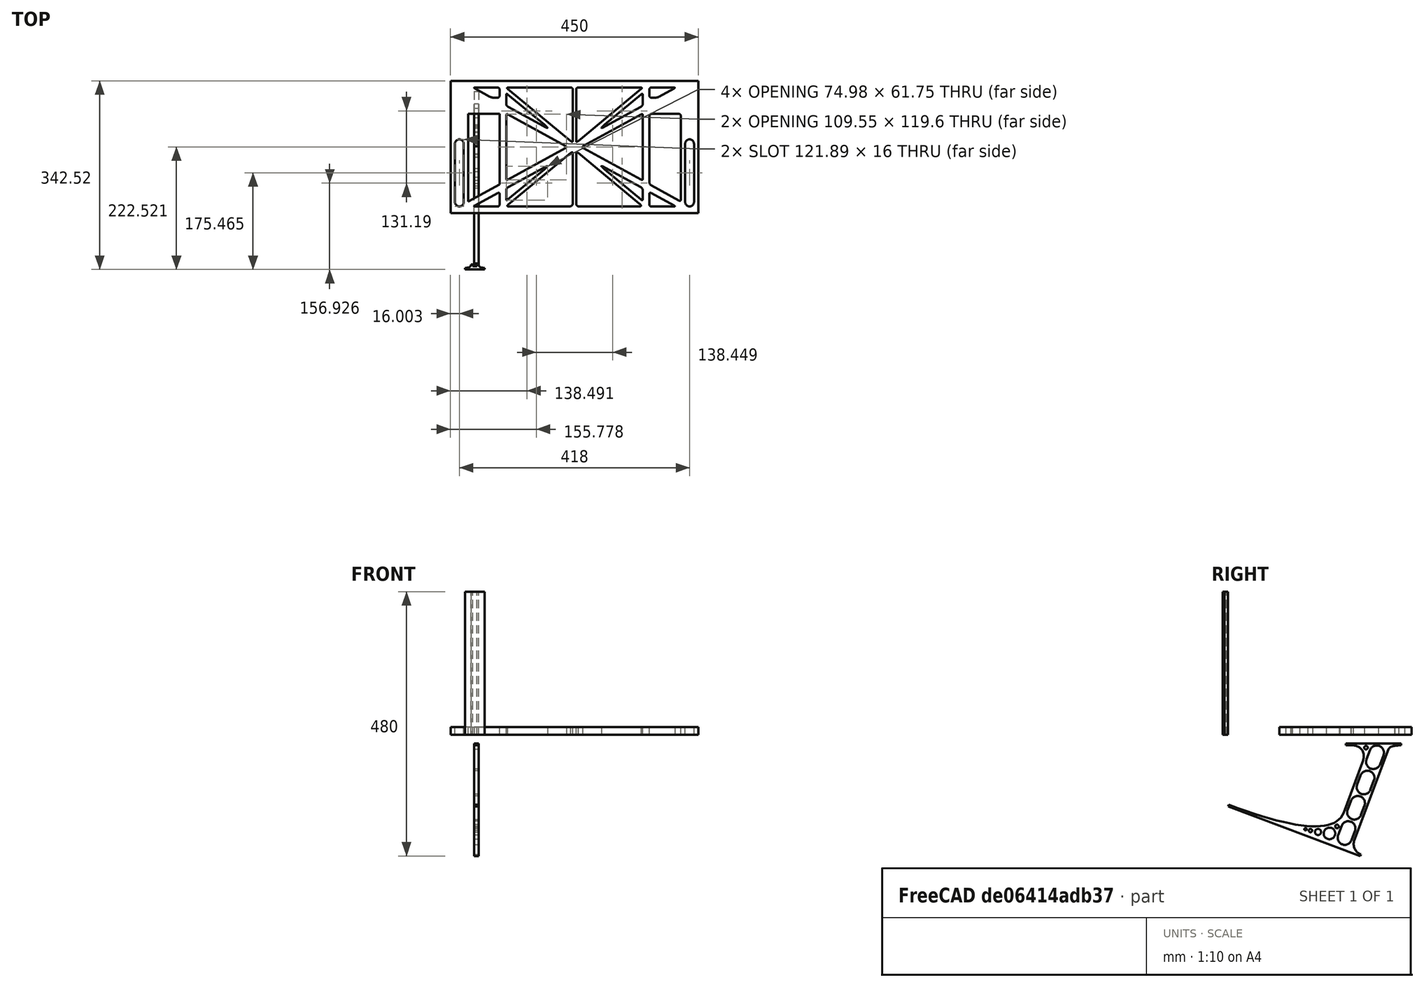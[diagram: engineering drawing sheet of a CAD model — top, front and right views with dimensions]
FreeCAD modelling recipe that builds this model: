
FCSTD DOCUMENT  (FreeCAD 0.19R0.19.2)
Label: laptopStand140FCStd
License: All rights reserved
LicenseURL: http://en.wikipedia.org/wiki/All_rights_reserved
objects: Sketcher::SketchObject×4, Part::Extrusion×3
note: 7 computed .brp shape members not serialized (recipe doc carries the construction recipe); baked Part::Feature solids carry a one-line shape summary decoded from their .brp

FEATURE [Sketcher::SketchObject] Sketch
  FullyConstrained = false
  sketch-geometry (349):
    g0: LineSegment StartX=-10.9272 StartY=-82.7794 StartZ=0 EndX=46.0728 EndY=-51.4823 EndZ=0
    g1: LineSegment StartX=-10.9272 StartY=76.4095 StartZ=0 EndX=-10.9272 EndY=-82.7794 EndZ=0
    g2: LineSegment StartX=46.0728 StartY=76.4095 StartZ=0 EndX=46.0728 EndY=-51.4823 EndZ=0
    g3: LineSegment StartX=-42.9272 StartY=136.221 StartZ=0 EndX=-42.9272 EndY=-103.779 EndZ=0
    g4: LineSegment StartX=407.073 StartY=136.221 StartZ=0 EndX=407.073 EndY=-103.779 EndZ=0
    g5: ArcOfCircle CenterX=-26.9272 CenterY=-83.7794 CenterZ=0 NormalX=0 NormalY=0 NormalZ=1 AngleXU=0 Radius=8 StartAngle=3.14159 EndAngle=6.28319
    g6: ArcOfCircle CenterX=391.073 CenterY=22.1087 CenterZ=0 NormalX=0 NormalY=0 NormalZ=1 AngleXU=0 Radius=8 StartAngle=-4.4e-15 EndAngle=3.14159
    g7: LineSegment StartX=399.073 StartY=22.1087 StartZ=0 EndX=399.073 EndY=-83.7794 EndZ=0
    g8: LineSegment StartX=383.073 StartY=22.1087 StartZ=0 EndX=383.073 EndY=-83.7794 EndZ=0
    g9: ArcOfCircle CenterX=391.073 CenterY=-83.7794 CenterZ=0 NormalX=0 NormalY=0 NormalZ=1 AngleXU=0 Radius=8 StartAngle=3.14159 EndAngle=6.28319
    g10: Circle CenterX=175.022 CenterY=27.0628 CenterZ=0 NormalX=0 NormalY=0 NormalZ=1 AngleXU=0 Radius=1
    g11: Circle CenterX=179.022 CenterY=24.8665 CenterZ=0 NormalX=0 NormalY=0 NormalZ=1 AngleXU=0 Radius=1
    g12: Circle CenterX=179.022 CenterY=27.0628 CenterZ=0 NormalX=0 NormalY=0 NormalZ=1 AngleXU=0 Radius=1
    g13: BSplineCurve PolesCount=3 KnotsCount=2 Degree=2 IsPeriodic=0
    g14: GeomPoint X=175.022 Y=27.0628 Z=0
    g15: GeomPoint X=179.022 Y=27.0628 Z=0
    g16: Circle CenterX=189.124 CenterY=27.0628 CenterZ=0 NormalX=0 NormalY=0 NormalZ=1 AngleXU=0 Radius=1
    g17: Circle CenterX=185.124 CenterY=24.8665 CenterZ=0 NormalX=0 NormalY=0 NormalZ=1 AngleXU=0 Radius=1
    g18: Circle CenterX=185.124 CenterY=27.0628 CenterZ=0 NormalX=0 NormalY=0 NormalZ=1 AngleXU=0 Radius=1
    g19: BSplineCurve PolesCount=3 KnotsCount=2 Degree=2 IsPeriodic=0
    g20: GeomPoint X=189.124 Y=27.0628 Z=0
    g21: GeomPoint X=185.124 Y=27.0628 Z=0
    g22: Circle CenterX=175.022 CenterY=5.37834 CenterZ=0 NormalX=0 NormalY=0 NormalZ=1 AngleXU=0 Radius=1
    g23: Circle CenterX=179.022 CenterY=7.57463 CenterZ=0 NormalX=0 NormalY=0 NormalZ=1 AngleXU=0 Radius=1
    g24: Circle CenterX=179.022 CenterY=5.34704 CenterZ=0 NormalX=0 NormalY=0 NormalZ=1 AngleXU=0 Radius=1
    g25: BSplineCurve PolesCount=3 KnotsCount=2 Degree=2 IsPeriodic=0
    g26: GeomPoint X=175.022 Y=5.37834 Z=0
    g27: GeomPoint X=179.022 Y=5.34704 Z=0
    g28: Circle CenterX=189.124 CenterY=5.37834 CenterZ=0 NormalX=0 NormalY=0 NormalZ=1 AngleXU=0 Radius=1
    g29: Circle CenterX=185.124 CenterY=7.57463 CenterZ=0 NormalX=0 NormalY=0 NormalZ=1 AngleXU=0 Radius=1
    g30: Circle CenterX=185.124 CenterY=5.34704 CenterZ=0 NormalX=0 NormalY=0 NormalZ=1 AngleXU=0 Radius=1
    g31: BSplineCurve PolesCount=3 KnotsCount=2 Degree=2 IsPeriodic=0
    g32: GeomPoint X=189.124 Y=5.37834 Z=0
    g33: GeomPoint X=185.124 Y=5.34704 Z=0
    g34: Circle CenterX=165.871 CenterY=18.1458 CenterZ=0 NormalX=0 NormalY=0 NormalZ=1 AngleXU=0 Radius=1
    g35: Circle CenterX=169.377 CenterY=16.2206 CenterZ=0 NormalX=0 NormalY=0 NormalZ=1 AngleXU=0 Radius=1
    g36: Circle CenterX=165.871 CenterY=14.2954 CenterZ=0 NormalX=0 NormalY=0 NormalZ=1 AngleXU=0 Radius=1
    g37: BSplineCurve PolesCount=3 KnotsCount=2 Degree=2 IsPeriodic=0
    g38: GeomPoint X=165.871 Y=18.1458 Z=0
    g39: GeomPoint X=165.871 Y=14.2954 Z=0
    g40: Circle CenterX=198.275 CenterY=18.1458 CenterZ=0 NormalX=0 NormalY=0 NormalZ=1 AngleXU=0 Radius=1
    g41: Circle CenterX=194.768 CenterY=16.2206 CenterZ=0 NormalX=0 NormalY=0 NormalZ=1 AngleXU=0 Radius=1
    g42: Circle CenterX=198.275 CenterY=14.2954 CenterZ=0 NormalX=0 NormalY=0 NormalZ=1 AngleXU=0 Radius=1
    g43: BSplineCurve PolesCount=3 KnotsCount=2 Degree=2 IsPeriodic=0
    g44: GeomPoint X=198.275 Y=18.1458 Z=0
    g45: GeomPoint X=198.275 Y=14.2954 Z=0
    g46: LineSegment StartX=407.073 StartY=-103.779 StartZ=0 EndX=-42.9272 EndY=-103.779 EndZ=0
    g47: LineSegment StartX=407.073 StartY=136.221 StartZ=0 EndX=-42.9272 EndY=136.221 EndZ=0
    g48: LineSegment StartX=46.0728 StartY=76.4095 StartZ=0 EndX=-10.9272 EndY=76.4095 EndZ=0
    g49: Circle CenterX=125.607 CenterY=54.1951 CenterZ=0 NormalX=0 NormalY=0 NormalZ=1 AngleXU=0 Radius=1
    g50: Circle CenterX=139.632 CenterY=46.4944 CenterZ=0 NormalX=0 NormalY=0 NormalZ=1 AngleXU=0 Radius=1
    g51: Circle CenterX=127.326 CenterY=56.7187 CenterZ=0 NormalX=0 NormalY=0 NormalZ=1 AngleXU=0 Radius=1
    g52: BSplineCurve PolesCount=3 KnotsCount=2 Degree=2 IsPeriodic=0
    g53: GeomPoint X=125.607 Y=54.1951 Z=0
    g54: GeomPoint X=127.326 Y=56.7187 Z=0
    g55: Circle CenterX=236.821 CenterY=56.7187 CenterZ=0 NormalX=0 NormalY=0 NormalZ=1 AngleXU=0 Radius=1
    g56: Circle CenterX=224.513 CenterY=46.4944 CenterZ=0 NormalX=0 NormalY=0 NormalZ=1 AngleXU=0 Radius=1
    g57: Circle CenterX=238.538 CenterY=54.1951 CenterZ=0 NormalX=0 NormalY=0 NormalZ=1 AngleXU=0 Radius=1
    g58: BSplineCurve PolesCount=3 KnotsCount=2 Degree=2 IsPeriodic=0
    g59: GeomPoint X=236.821 Y=56.7187 Z=0
    g60: GeomPoint X=238.538 Y=54.1951 Z=0
    g61: Circle CenterX=238.538 CenterY=-21.7539 CenterZ=0 NormalX=0 NormalY=0 NormalZ=1 AngleXU=0 Radius=1
    g62: Circle CenterX=224.513 CenterY=-14.0532 CenterZ=0 NormalX=0 NormalY=0 NormalZ=1 AngleXU=0 Radius=1
    g63: Circle CenterX=236.821 CenterY=-24.2775 CenterZ=0 NormalX=0 NormalY=0 NormalZ=1 AngleXU=0 Radius=1
    g64: BSplineCurve PolesCount=3 KnotsCount=2 Degree=2 IsPeriodic=0
    g65: GeomPoint X=238.538 Y=-21.7539 Z=0
    g66: GeomPoint X=236.821 Y=-24.2775 Z=0
    g67: Circle CenterX=125.607 CenterY=-21.7539 CenterZ=0 NormalX=0 NormalY=0 NormalZ=1 AngleXU=0 Radius=1
    g68: Circle CenterX=139.632 CenterY=-14.0532 CenterZ=0 NormalX=0 NormalY=0 NormalZ=1 AngleXU=0 Radius=1
    g69: Circle CenterX=127.325 CenterY=-24.2775 CenterZ=0 NormalX=0 NormalY=0 NormalZ=1 AngleXU=0 Radius=1
    g70: BSplineCurve PolesCount=3 KnotsCount=2 Degree=2 IsPeriodic=0
    g71: GeomPoint X=125.607 Y=-21.7539 Z=0
    g72: GeomPoint X=127.325 Y=-24.2775 Z=0
    g73: Circle CenterX=302.996 CenterY=111.695 CenterZ=0 NormalX=0 NormalY=0 NormalZ=1 AngleXU=0 Radius=1
    g74: Circle CenterX=306.073 CenterY=114.251 CenterZ=0 NormalX=0 NormalY=0 NormalZ=1 AngleXU=0 Radius=1
    g75: Circle CenterX=306.073 CenterY=110.251 CenterZ=0 NormalX=0 NormalY=0 NormalZ=1 AngleXU=0 Radius=1
    g76: BSplineCurve PolesCount=3 KnotsCount=2 Degree=2 IsPeriodic=0
    g77: GeomPoint X=302.996 Y=111.695 Z=0
    g78: GeomPoint X=306.073 Y=110.251 Z=0
    g79: Circle CenterX=306.073 CenterY=95.2763 CenterZ=0 NormalX=0 NormalY=0 NormalZ=1 AngleXU=0 Radius=1
    g80: Circle CenterX=306.073 CenterY=91.2763 CenterZ=0 NormalX=0 NormalY=0 NormalZ=1 AngleXU=0 Radius=1
    g81: Circle CenterX=302.567 CenterY=89.3511 CenterZ=0 NormalX=0 NormalY=0 NormalZ=1 AngleXU=0 Radius=1
    g82: BSplineCurve PolesCount=3 KnotsCount=2 Degree=2 IsPeriodic=0
    g83: GeomPoint X=306.073 Y=95.2763 Z=0
    g84: GeomPoint X=302.567 Y=89.3511 Z=0
    g85: LineSegment StartX=306.073 StartY=110.251 StartZ=0 EndX=306.073 EndY=95.2763 EndZ=0
    g86: LineSegment StartX=302.996 StartY=111.695 StartZ=0 EndX=236.821 EndY=56.7187 EndZ=0
    g87: LineSegment StartX=238.538 StartY=54.1951 StartZ=0 EndX=302.567 EndY=89.3511 EndZ=0
    g88: Circle CenterX=61.1496 CenterY=111.695 CenterZ=0 NormalX=0 NormalY=0 NormalZ=1 AngleXU=0 Radius=1
    g89: Circle CenterX=58.0728 CenterY=114.251 CenterZ=0 NormalX=0 NormalY=0 NormalZ=1 AngleXU=0 Radius=1
    g90: Circle CenterX=58.0728 CenterY=110.251 CenterZ=0 NormalX=0 NormalY=0 NormalZ=1 AngleXU=0 Radius=1
    g91: BSplineCurve PolesCount=3 KnotsCount=2 Degree=2 IsPeriodic=0
    g92: GeomPoint X=61.1496 Y=111.695 Z=0
    g93: GeomPoint X=58.0728 Y=110.251 Z=0
    g94: Circle CenterX=61.5791 CenterY=89.3511 CenterZ=0 NormalX=0 NormalY=0 NormalZ=1 AngleXU=0 Radius=1
    g95: Circle CenterX=58.0728 CenterY=91.2763 CenterZ=0 NormalX=0 NormalY=0 NormalZ=1 AngleXU=0 Radius=1
    g96: Circle CenterX=58.0728 CenterY=95.2763 CenterZ=0 NormalX=0 NormalY=0 NormalZ=1 AngleXU=0 Radius=1
    g97: BSplineCurve PolesCount=3 KnotsCount=2 Degree=2 IsPeriodic=0
    g98: GeomPoint X=61.5791 Y=89.3511 Z=0
    g99: GeomPoint X=58.0728 Y=95.2763 Z=0
    g100: LineSegment StartX=58.0728 StartY=110.251 StartZ=0 EndX=58.0728 EndY=95.2763 EndZ=0
    g101: LineSegment StartX=61.1496 StartY=111.695 StartZ=0 EndX=127.326 EndY=56.7187 EndZ=0
    g102: LineSegment StartX=125.607 StartY=54.1951 StartZ=0 EndX=61.5791 EndY=89.3511 EndZ=0
    g103: Circle CenterX=61.5791 CenterY=-56.9099 CenterZ=0 NormalX=0 NormalY=0 NormalZ=1 AngleXU=0 Radius=1
    g104: Circle CenterX=58.0728 CenterY=-58.8351 CenterZ=0 NormalX=0 NormalY=0 NormalZ=1 AngleXU=0 Radius=1
    g105: Circle CenterX=58.0728 CenterY=-62.8351 CenterZ=0 NormalX=0 NormalY=0 NormalZ=1 AngleXU=0 Radius=1
    g106: BSplineCurve PolesCount=3 KnotsCount=2 Degree=2 IsPeriodic=0
    g107: GeomPoint X=61.5791 Y=-56.9099 Z=0
    g108: GeomPoint X=58.0728 Y=-62.8351 Z=0
    g109: Circle CenterX=58.0728 CenterY=-77.8102 CenterZ=0 NormalX=0 NormalY=0 NormalZ=1 AngleXU=0 Radius=1
    g110: Circle CenterX=58.0728 CenterY=-81.8102 CenterZ=0 NormalX=0 NormalY=0 NormalZ=1 AngleXU=0 Radius=1
    g111: Circle CenterX=61.1496 CenterY=-79.2541 CenterZ=0 NormalX=0 NormalY=0 NormalZ=1 AngleXU=0 Radius=1
    g112: BSplineCurve PolesCount=3 KnotsCount=2 Degree=2 IsPeriodic=0
    g113: GeomPoint X=58.0728 Y=-77.8102 Z=0
    g114: GeomPoint X=61.1496 Y=-79.2541 Z=0
    g115: LineSegment StartX=58.0728 StartY=-62.8351 StartZ=0 EndX=58.0728 EndY=-77.8102 EndZ=0
    g116: LineSegment StartX=61.1496 StartY=-79.2541 StartZ=0 EndX=127.325 EndY=-24.2775 EndZ=0
    g117: LineSegment StartX=125.607 StartY=-21.7539 StartZ=0 EndX=61.5791 EndY=-56.9099 EndZ=0
    g118: Circle CenterX=302.567 CenterY=-56.9099 CenterZ=0 NormalX=0 NormalY=0 NormalZ=1 AngleXU=0 Radius=1
    g119: Circle CenterX=306.073 CenterY=-58.8351 CenterZ=0 NormalX=0 NormalY=0 NormalZ=1 AngleXU=0 Radius=1
    g120: Circle CenterX=306.073 CenterY=-62.8351 CenterZ=0 NormalX=0 NormalY=0 NormalZ=1 AngleXU=0 Radius=1
    g121: BSplineCurve PolesCount=3 KnotsCount=2 Degree=2 IsPeriodic=0
    g122: GeomPoint X=302.567 Y=-56.9099 Z=0
    g123: GeomPoint X=306.073 Y=-62.8351 Z=0
    g124: Circle CenterX=302.996 CenterY=-79.2541 CenterZ=0 NormalX=0 NormalY=0 NormalZ=1 AngleXU=0 Radius=1
    g125: Circle CenterX=306.073 CenterY=-81.8102 CenterZ=0 NormalX=0 NormalY=0 NormalZ=1 AngleXU=0 Radius=1
    g126: Circle CenterX=306.073 CenterY=-77.8102 CenterZ=0 NormalX=0 NormalY=0 NormalZ=1 AngleXU=0 Radius=1
    g127: BSplineCurve PolesCount=3 KnotsCount=2 Degree=2 IsPeriodic=0
    g128: GeomPoint X=302.996 Y=-79.2541 Z=0
    g129: GeomPoint X=306.073 Y=-77.8102 Z=0
    g130: LineSegment StartX=306.073 StartY=-62.8351 StartZ=0 EndX=306.073 EndY=-77.8102 EndZ=0
    g131: LineSegment StartX=302.996 StartY=-79.2541 StartZ=0 EndX=236.821 EndY=-24.2775 EndZ=0
    g132: LineSegment StartX=238.538 StartY=-21.7539 StartZ=0 EndX=302.567 EndY=-56.9099 EndZ=0
    g133: Circle CenterX=61.6457 CenterY=-88.8112 CenterZ=0 NormalX=0 NormalY=0 NormalZ=1 AngleXU=0 Radius=1
    g134: Circle CenterX=58.0728 CenterY=-91.7794 CenterZ=0 NormalX=0 NormalY=0 NormalZ=1 AngleXU=0 Radius=1
    g135: Circle CenterX=63.9135 CenterY=-91.7794 CenterZ=0 NormalX=0 NormalY=0 NormalZ=1 AngleXU=0 Radius=1
    g136: BSplineCurve PolesCount=3 KnotsCount=2 Degree=2 IsPeriodic=0
    g137: GeomPoint X=61.6457 Y=-88.8112 Z=0
    g138: GeomPoint X=63.9135 Y=-91.7794 Z=0
    g139: Circle CenterX=179.022 CenterY=-85.8163 CenterZ=0 NormalX=0 NormalY=0 NormalZ=1 AngleXU=0 Radius=1
    g140: Circle CenterX=179.022 CenterY=-91.7794 CenterZ=0 NormalX=0 NormalY=0 NormalZ=1 AngleXU=0 Radius=1
    g141: Circle CenterX=171.895 CenterY=-91.7794 CenterZ=0 NormalX=0 NormalY=0 NormalZ=1 AngleXU=0 Radius=1
    g142: BSplineCurve PolesCount=3 KnotsCount=2 Degree=2 IsPeriodic=0
    g143: GeomPoint X=179.022 Y=-85.8163 Z=0
    g144: GeomPoint X=171.895 Y=-91.7794 Z=0
    g145: Circle CenterX=185.124 CenterY=-86.2028 CenterZ=0 NormalX=0 NormalY=0 NormalZ=1 AngleXU=0 Radius=1
    g146: Circle CenterX=185.124 CenterY=-91.7794 CenterZ=0 NormalX=0 NormalY=0 NormalZ=1 AngleXU=0 Radius=1
    g147: Circle CenterX=191.747 CenterY=-91.7794 CenterZ=0 NormalX=0 NormalY=0 NormalZ=1 AngleXU=0 Radius=1
    g148: BSplineCurve PolesCount=3 KnotsCount=2 Degree=2 IsPeriodic=0
    g149: GeomPoint X=185.124 Y=-86.2028 Z=0
    g150: GeomPoint X=191.747 Y=-91.7794 Z=0
    g151: Circle CenterX=299.888 CenterY=-86.6413 CenterZ=0 NormalX=0 NormalY=0 NormalZ=1 AngleXU=0 Radius=1
    g152: Circle CenterX=306.073 CenterY=-91.7794 CenterZ=0 NormalX=0 NormalY=0 NormalZ=1 AngleXU=0 Radius=1
    g153: Circle CenterX=298.776 CenterY=-91.7794 CenterZ=0 NormalX=0 NormalY=0 NormalZ=1 AngleXU=0 Radius=1
    g154: BSplineCurve PolesCount=3 KnotsCount=2 Degree=2 IsPeriodic=0
    g155: GeomPoint X=299.888 Y=-86.6413 Z=0
    g156: GeomPoint X=298.776 Y=-91.7794 Z=0
    g157: LineSegment StartX=189.124 StartY=5.37834 StartZ=0 EndX=299.888 EndY=-86.6413 EndZ=0
    g158: LineSegment StartX=298.776 StartY=-91.7794 StartZ=0 EndX=191.747 EndY=-91.7794 EndZ=0
    g159: LineSegment StartX=185.124 StartY=-86.2028 StartZ=0 EndX=185.124 EndY=5.34704 EndZ=0
    g160: LineSegment StartX=179.022 StartY=5.34704 StartZ=0 EndX=179.022 EndY=-85.8163 EndZ=0
    g161: LineSegment StartX=171.895 StartY=-91.7794 StartZ=0 EndX=63.9135 EndY=-91.7794 EndZ=0
    g162: LineSegment StartX=61.6457 StartY=-88.8112 StartZ=0 EndX=175.022 EndY=5.37834 EndZ=0
    g163: Circle CenterX=302.073 CenterY=124.221 CenterZ=0 NormalX=0 NormalY=0 NormalZ=1 AngleXU=0 Radius=1
    g164: Circle CenterX=306.073 CenterY=124.221 CenterZ=0 NormalX=0 NormalY=0 NormalZ=1 AngleXU=0 Radius=1
    g165: Circle CenterX=302.996 CenterY=121.665 CenterZ=0 NormalX=0 NormalY=0 NormalZ=1 AngleXU=0 Radius=1
    g166: BSplineCurve PolesCount=3 KnotsCount=2 Degree=2 IsPeriodic=0
    g167: GeomPoint X=302.073 Y=124.221 Z=0
    g168: GeomPoint X=302.996 Y=121.665 Z=0
    g169: Circle CenterX=189.124 CenterY=124.221 CenterZ=0 NormalX=0 NormalY=0 NormalZ=1 AngleXU=0 Radius=1
    g170: Circle CenterX=185.124 CenterY=124.221 CenterZ=0 NormalX=0 NormalY=0 NormalZ=1 AngleXU=0 Radius=1
    g171: Circle CenterX=185.124 CenterY=120.221 CenterZ=0 NormalX=0 NormalY=0 NormalZ=1 AngleXU=0 Radius=1
    g172: BSplineCurve PolesCount=3 KnotsCount=2 Degree=2 IsPeriodic=0
    g173: GeomPoint X=189.124 Y=124.221 Z=0
    g174: GeomPoint X=185.124 Y=120.221 Z=0
    g175: Circle CenterX=175.022 CenterY=124.221 CenterZ=0 NormalX=0 NormalY=0 NormalZ=1 AngleXU=0 Radius=1
    g176: Circle CenterX=179.022 CenterY=124.221 CenterZ=0 NormalX=0 NormalY=0 NormalZ=1 AngleXU=0 Radius=1
    g177: Circle CenterX=179.022 CenterY=120.221 CenterZ=0 NormalX=0 NormalY=0 NormalZ=1 AngleXU=0 Radius=1
    g178: BSplineCurve PolesCount=3 KnotsCount=2 Degree=2 IsPeriodic=0
    g179: GeomPoint X=175.022 Y=124.221 Z=0
    g180: GeomPoint X=179.022 Y=120.221 Z=0
    g181: Circle CenterX=62.0728 CenterY=124.221 CenterZ=0 NormalX=0 NormalY=0 NormalZ=1 AngleXU=0 Radius=1
    g182: Circle CenterX=58.0728 CenterY=124.221 CenterZ=0 NormalX=0 NormalY=0 NormalZ=1 AngleXU=0 Radius=1
    g183: Circle CenterX=61.1496 CenterY=121.665 CenterZ=0 NormalX=0 NormalY=0 NormalZ=1 AngleXU=0 Radius=1
    g184: BSplineCurve PolesCount=3 KnotsCount=2 Degree=2 IsPeriodic=0
    g185: GeomPoint X=62.0728 Y=124.221 Z=0
    g186: GeomPoint X=61.1496 Y=121.665 Z=0
    g187: LineSegment StartX=62.0728 StartY=124.221 StartZ=0 EndX=175.022 EndY=124.221 EndZ=0
    g188: LineSegment StartX=179.022 StartY=120.221 StartZ=0 EndX=179.022 EndY=27.0628 EndZ=0
    g189: LineSegment StartX=185.124 StartY=27.0628 StartZ=0 EndX=185.124 EndY=120.221 EndZ=0
    g190: LineSegment StartX=189.124 StartY=124.221 StartZ=0 EndX=302.073 EndY=124.221 EndZ=0
    g191: LineSegment StartX=302.996 StartY=121.665 StartZ=0 EndX=189.124 EndY=27.0628 EndZ=0
    g192: LineSegment StartX=175.022 StartY=27.0628 StartZ=0 EndX=61.1496 EndY=121.665 EndZ=0
    g193: Circle CenterX=61.5791 CenterY=75.4095 CenterZ=0 NormalX=0 NormalY=0 NormalZ=1 AngleXU=0 Radius=1
    g194: Circle CenterX=58.0728 CenterY=77.3346 CenterZ=0 NormalX=0 NormalY=0 NormalZ=1 AngleXU=0 Radius=1
    g195: Circle CenterX=58.0728 CenterY=73.3346 CenterZ=0 NormalX=0 NormalY=0 NormalZ=1 AngleXU=0 Radius=1
    g196: BSplineCurve PolesCount=3 KnotsCount=2 Degree=2 IsPeriodic=0
    g197: GeomPoint X=61.5791 Y=75.4095 Z=0
    g198: GeomPoint X=58.0728 Y=73.3346 Z=0
    g199: Circle CenterX=58.0728 CenterY=-40.8935 CenterZ=0 NormalX=0 NormalY=0 NormalZ=1 AngleXU=0 Radius=1
    g200: Circle CenterX=58.0728 CenterY=-44.8935 CenterZ=0 NormalX=0 NormalY=0 NormalZ=1 AngleXU=0 Radius=1
    g201: Circle CenterX=61.5791 CenterY=-42.9683 CenterZ=0 NormalX=0 NormalY=0 NormalZ=1 AngleXU=0 Radius=1
    g202: BSplineCurve PolesCount=3 KnotsCount=2 Degree=2 IsPeriodic=0
    g203: GeomPoint X=58.0728 Y=-40.8935 Z=0
    g204: GeomPoint X=61.5791 Y=-42.9683 Z=0
    g205: LineSegment StartX=61.5791 StartY=-42.9683 StartZ=0 EndX=165.871 EndY=14.2954 EndZ=0
    g206: LineSegment StartX=165.871 StartY=18.1458 StartZ=0 EndX=61.5791 EndY=75.4095 EndZ=0
    g207: LineSegment StartX=58.0728 StartY=73.3346 StartZ=0 EndX=58.0728 EndY=-40.8935 EndZ=0
    g208: Circle CenterX=302.567 CenterY=-42.9683 CenterZ=0 NormalX=0 NormalY=0 NormalZ=1 AngleXU=0 Radius=1
    g209: Circle CenterX=306.073 CenterY=-44.8935 CenterZ=0 NormalX=0 NormalY=0 NormalZ=1 AngleXU=0 Radius=1
    g210: Circle CenterX=306.073 CenterY=-40.8935 CenterZ=0 NormalX=0 NormalY=0 NormalZ=1 AngleXU=0 Radius=1
    g211: BSplineCurve PolesCount=3 KnotsCount=2 Degree=2 IsPeriodic=0
    g212: GeomPoint X=302.567 Y=-42.9683 Z=0
    g213: GeomPoint X=306.073 Y=-40.8935 Z=0
    g214: Circle CenterX=306.073 CenterY=73.3346 CenterZ=0 NormalX=0 NormalY=0 NormalZ=1 AngleXU=0 Radius=1
    g215: Circle CenterX=306.073 CenterY=77.3346 CenterZ=0 NormalX=0 NormalY=0 NormalZ=1 AngleXU=0 Radius=1
    g216: Circle CenterX=302.567 CenterY=75.4095 CenterZ=0 NormalX=0 NormalY=0 NormalZ=1 AngleXU=0 Radius=1
    g217: BSplineCurve PolesCount=3 KnotsCount=2 Degree=2 IsPeriodic=0
    g218: GeomPoint X=306.073 Y=73.3346 Z=0
    g219: GeomPoint X=302.567 Y=75.4095 Z=0
    g220: LineSegment StartX=302.567 StartY=-42.9683 StartZ=0 EndX=198.275 EndY=14.2954 EndZ=0
    g221: LineSegment StartX=198.275 StartY=18.1458 StartZ=0 EndX=302.567 EndY=75.4095 EndZ=0
    g222: LineSegment StartX=306.073 StartY=73.3346 StartZ=0 EndX=306.073 EndY=-40.8935 EndZ=0
    g223: LineSegment StartX=322.073 StartY=105.865 StartZ=0 EndX=328.643 EndY=105.865 EndZ=0
    g224: LineSegment StartX=318.073 StartY=120.221 StartZ=0 EndX=318.073 EndY=109.865 EndZ=0
    g225: LineSegment StartX=336.157 StartY=107.779 StartZ=0 EndX=362.567 EndY=122.294 EndZ=0
    g226: Circle CenterX=362.073 CenterY=124.221 CenterZ=0 NormalX=0 NormalY=0 NormalZ=1 AngleXU=0 Radius=1
    g227: Circle CenterX=366.073 CenterY=124.221 CenterZ=0 NormalX=0 NormalY=0 NormalZ=1 AngleXU=0 Radius=1
    g228: Circle CenterX=362.567 CenterY=122.294 CenterZ=0 NormalX=0 NormalY=0 NormalZ=1 AngleXU=0 Radius=1
    g229: BSplineCurve PolesCount=3 KnotsCount=2 Degree=2 IsPeriodic=0
    g230: GeomPoint X=362.073 Y=124.221 Z=0
    g231: GeomPoint X=362.567 Y=122.294 Z=0
    g232: Circle CenterX=322.073 CenterY=124.221 CenterZ=0 NormalX=0 NormalY=0 NormalZ=1 AngleXU=0 Radius=1
    g233: Circle CenterX=318.073 CenterY=124.221 CenterZ=0 NormalX=0 NormalY=0 NormalZ=1 AngleXU=0 Radius=1
    g234: Circle CenterX=318.073 CenterY=120.221 CenterZ=0 NormalX=0 NormalY=0 NormalZ=1 AngleXU=0 Radius=1
    g235: BSplineCurve PolesCount=3 KnotsCount=2 Degree=2 IsPeriodic=0
    g236: GeomPoint X=322.073 Y=124.221 Z=0
    g237: GeomPoint X=318.073 Y=120.221 Z=0
    g238: Circle CenterX=322.073 CenterY=105.865 CenterZ=0 NormalX=0 NormalY=0 NormalZ=1 AngleXU=0 Radius=1
    g239: Circle CenterX=318.073 CenterY=105.865 CenterZ=0 NormalX=0 NormalY=0 NormalZ=1 AngleXU=0 Radius=1
    g240: Circle CenterX=318.073 CenterY=109.865 CenterZ=0 NormalX=0 NormalY=0 NormalZ=1 AngleXU=0 Radius=1
    g241: BSplineCurve PolesCount=3 KnotsCount=2 Degree=2 IsPeriodic=0
    g242: GeomPoint X=322.073 Y=105.865 Z=0
    g243: GeomPoint X=318.073 Y=109.865 Z=0
    g244: Circle CenterX=336.157 CenterY=107.779 CenterZ=0 NormalX=0 NormalY=0 NormalZ=1 AngleXU=0 Radius=1
    g245: Circle CenterX=332.651 CenterY=105.853 CenterZ=0 NormalX=0 NormalY=0 NormalZ=1 AngleXU=0 Radius=1
    g246: Circle CenterX=328.643 CenterY=105.865 CenterZ=0 NormalX=0 NormalY=0 NormalZ=1 AngleXU=0 Radius=1
    g247: BSplineCurve PolesCount=3 KnotsCount=2 Degree=2 IsPeriodic=0
    g248: GeomPoint X=336.157 Y=107.779 Z=0
    g249: GeomPoint X=328.643 Y=105.865 Z=0
    g250: LineSegment StartX=322.073 StartY=124.221 StartZ=0 EndX=362.073 EndY=124.221 EndZ=0
    g251: Circle CenterX=371.567 CenterY=-80.8644 CenterZ=0 NormalX=0 NormalY=0 NormalZ=1 AngleXU=0 Radius=1
    g252: Circle CenterX=375.073 CenterY=-82.7896 CenterZ=0 NormalX=0 NormalY=0 NormalZ=1 AngleXU=0 Radius=1
    g253: Circle CenterX=375.073 CenterY=-78.7896 CenterZ=0 NormalX=0 NormalY=0 NormalZ=1 AngleXU=0 Radius=1
    g254: BSplineCurve PolesCount=3 KnotsCount=2 Degree=2 IsPeriodic=0
    g255: GeomPoint X=371.567 Y=-80.8644 Z=0
    g256: GeomPoint X=375.073 Y=-78.7896 Z=0
    g257: Circle CenterX=321.579 CenterY=-53.4075 CenterZ=0 NormalX=0 NormalY=0 NormalZ=1 AngleXU=0 Radius=1
    g258: Circle CenterX=318.073 CenterY=-51.4823 CenterZ=0 NormalX=0 NormalY=0 NormalZ=1 AngleXU=0 Radius=1
    g259: Circle CenterX=318.073 CenterY=-47.4805 CenterZ=0 NormalX=0 NormalY=0 NormalZ=1 AngleXU=0 Radius=1
    g260: BSplineCurve PolesCount=3 KnotsCount=2 Degree=2 IsPeriodic=0
    g261: GeomPoint X=321.579 Y=-53.4075 Z=0
    g262: GeomPoint X=318.073 Y=-47.4805 Z=0
    g263: LineSegment StartX=371.567 StartY=-80.8644 StartZ=0 EndX=321.579 EndY=-53.4075 EndZ=0
    g264: Circle CenterX=321.579 CenterY=-67.3492 CenterZ=0 NormalX=0 NormalY=0 NormalZ=1 AngleXU=0 Radius=1
    g265: Circle CenterX=318.073 CenterY=-65.424 CenterZ=0 NormalX=0 NormalY=0 NormalZ=1 AngleXU=0 Radius=1
    g266: Circle CenterX=318.073 CenterY=-69.424 CenterZ=0 NormalX=0 NormalY=0 NormalZ=1 AngleXU=0 Radius=1
    g267: BSplineCurve PolesCount=3 KnotsCount=2 Degree=2 IsPeriodic=0
    g268: GeomPoint X=321.579 Y=-67.3492 Z=0
    g269: GeomPoint X=318.073 Y=-69.424 Z=0
    g270: Circle CenterX=362.567 CenterY=-89.8542 CenterZ=0 NormalX=0 NormalY=0 NormalZ=1 AngleXU=0 Radius=1
    g271: Circle CenterX=366.073 CenterY=-91.7794 CenterZ=0 NormalX=0 NormalY=0 NormalZ=1 AngleXU=0 Radius=1
    g272: Circle CenterX=362.073 CenterY=-91.7794 CenterZ=0 NormalX=0 NormalY=0 NormalZ=1 AngleXU=0 Radius=1
    g273: BSplineCurve PolesCount=3 KnotsCount=2 Degree=2 IsPeriodic=0
    g274: GeomPoint X=362.567 Y=-89.8542 Z=0
    g275: GeomPoint X=362.073 Y=-91.7794 Z=0
    g276: Circle CenterX=322.073 CenterY=-91.7794 CenterZ=0 NormalX=0 NormalY=0 NormalZ=1 AngleXU=0 Radius=1
    g277: Circle CenterX=318.073 CenterY=-91.7794 CenterZ=0 NormalX=0 NormalY=0 NormalZ=1 AngleXU=0 Radius=1
    g278: Circle CenterX=318.073 CenterY=-87.7794 CenterZ=0 NormalX=0 NormalY=0 NormalZ=1 AngleXU=0 Radius=1
    g279: BSplineCurve PolesCount=3 KnotsCount=2 Degree=2 IsPeriodic=0
    g280: GeomPoint X=322.073 Y=-91.7794 Z=0
    g281: GeomPoint X=318.073 Y=-87.7794 Z=0
    g282: LineSegment StartX=362.567 StartY=-89.8542 StartZ=0 EndX=321.579 EndY=-67.3492 EndZ=0
    g283: LineSegment StartX=318.073 StartY=-69.424 StartZ=0 EndX=318.073 EndY=-87.7794 EndZ=0
    g284: LineSegment StartX=322.073 StartY=-91.7794 StartZ=0 EndX=362.073 EndY=-91.7794 EndZ=0
    g285: Circle CenterX=2.07281 CenterY=124.221 CenterZ=0 NormalX=0 NormalY=0 NormalZ=1 AngleXU=0 Radius=1
    g286: Circle CenterX=1.57905 CenterY=122.295 CenterZ=0 NormalX=0 NormalY=0 NormalZ=1 AngleXU=0 Radius=1
    g287: BSplineCurve PolesCount=3 KnotsCount=2 Degree=2 IsPeriodic=0
    g288: GeomPoint X=2.07281 Y=124.221 Z=0
    g289: GeomPoint X=1.57905 Y=122.295 Z=0
    g290: Circle CenterX=42.0728 CenterY=124.221 CenterZ=0 NormalX=0 NormalY=0 NormalZ=1 AngleXU=0 Radius=1
    g291: Circle CenterX=46.0728 CenterY=124.221 CenterZ=0 NormalX=0 NormalY=0 NormalZ=1 AngleXU=0 Radius=1
    g292: Circle CenterX=46.0728 CenterY=120.221 CenterZ=0 NormalX=0 NormalY=0 NormalZ=1 AngleXU=0 Radius=1
    g293: BSplineCurve PolesCount=3 KnotsCount=2 Degree=2 IsPeriodic=0
    g294: GeomPoint X=42.0728 Y=124.221 Z=0
    g295: GeomPoint X=46.0728 Y=120.221 Z=0
    g296: Circle CenterX=46.0728 CenterY=109.865 CenterZ=0 NormalX=0 NormalY=0 NormalZ=1 AngleXU=0 Radius=1
    g297: Circle CenterX=46.0728 CenterY=105.865 CenterZ=0 NormalX=0 NormalY=0 NormalZ=1 AngleXU=0 Radius=1
    g298: Circle CenterX=42.0728 CenterY=105.865 CenterZ=0 NormalX=0 NormalY=0 NormalZ=1 AngleXU=0 Radius=1
    g299: BSplineCurve PolesCount=3 KnotsCount=2 Degree=2 IsPeriodic=0
    g300: GeomPoint X=46.0728 Y=109.865 Z=0
    g301: GeomPoint X=42.0728 Y=105.865 Z=0
    g302: Circle CenterX=35.5028 CenterY=105.865 CenterZ=0 NormalX=0 NormalY=0 NormalZ=1 AngleXU=0 Radius=1
    g303: Circle CenterX=31.5028 CenterY=105.865 CenterZ=0 NormalX=0 NormalY=0 NormalZ=1 AngleXU=0 Radius=1
    g304: Circle CenterX=27.9965 CenterY=107.79 CenterZ=0 NormalX=0 NormalY=0 NormalZ=1 AngleXU=0 Radius=1
    g305: BSplineCurve PolesCount=3 KnotsCount=2 Degree=2 IsPeriodic=0
    g306: GeomPoint X=35.5028 Y=105.865 Z=0
    g307: GeomPoint X=27.9965 Y=107.79 Z=0
    g308: LineSegment StartX=2.07281 StartY=124.221 StartZ=0 EndX=42.0728 EndY=124.221 EndZ=0
    g309: LineSegment StartX=46.0728 StartY=120.221 StartZ=0 EndX=46.0728 EndY=109.865 EndZ=0
    g310: LineSegment StartX=42.0728 StartY=105.865 StartZ=0 EndX=35.5028 EndY=105.865 EndZ=0
    g311: LineSegment StartX=27.9965 StartY=107.79 StartZ=0 EndX=1.57905 EndY=122.295 EndZ=0
    g312: Circle CenterX=42.5666 CenterY=-67.3492 CenterZ=0 NormalX=0 NormalY=0 NormalZ=1 AngleXU=0 Radius=1
    g313: Circle CenterX=46.0728 CenterY=-65.424 CenterZ=0 NormalX=0 NormalY=0 NormalZ=1 AngleXU=0 Radius=1
    g314: Circle CenterX=46.0728 CenterY=-69.424 CenterZ=0 NormalX=0 NormalY=0 NormalZ=1 AngleXU=0 Radius=1
    g315: BSplineCurve PolesCount=3 KnotsCount=2 Degree=2 IsPeriodic=0
    g316: GeomPoint X=42.5666 Y=-67.3492 Z=0
    g317: GeomPoint X=46.0728 Y=-69.424 Z=0
    g318: Circle CenterX=46.0728 CenterY=-87.7794 CenterZ=0 NormalX=0 NormalY=0 NormalZ=1 AngleXU=0 Radius=1
    g319: Circle CenterX=46.0728 CenterY=-91.7794 CenterZ=0 NormalX=0 NormalY=0 NormalZ=1 AngleXU=0 Radius=1
    g320: Circle CenterX=42.0728 CenterY=-91.7794 CenterZ=0 NormalX=0 NormalY=0 NormalZ=1 AngleXU=0 Radius=1
    g321: BSplineCurve PolesCount=3 KnotsCount=2 Degree=2 IsPeriodic=0
    g322: GeomPoint X=46.0728 Y=-87.7794 Z=0
    g323: GeomPoint X=42.0728 Y=-91.7794 Z=0
    g324: Circle CenterX=2.07281 CenterY=-91.7794 CenterZ=0 NormalX=0 NormalY=0 NormalZ=1 AngleXU=0 Radius=1
    g325: Circle CenterX=-1.92719 CenterY=-91.7794 CenterZ=0 NormalX=0 NormalY=0 NormalZ=1 AngleXU=0 Radius=1
    g326: Circle CenterX=1.57905 CenterY=-89.8542 CenterZ=0 NormalX=0 NormalY=0 NormalZ=1 AngleXU=0 Radius=1
    g327: BSplineCurve PolesCount=3 KnotsCount=2 Degree=2 IsPeriodic=0
    g328: GeomPoint X=2.07281 Y=-91.7794 Z=0
    g329: GeomPoint X=1.57905 Y=-89.8542 Z=0
    g330: LineSegment StartX=2.07281 StartY=-91.7794 StartZ=0 EndX=42.0728 EndY=-91.7794 EndZ=0
    g331: LineSegment StartX=46.0728 StartY=-87.7794 StartZ=0 EndX=46.0728 EndY=-69.424 EndZ=0
    g332: LineSegment StartX=42.5666 StartY=-67.3492 StartZ=0 EndX=1.57905 EndY=-89.8542 EndZ=0
    g333: Circle CenterX=322.073 CenterY=76.4095 CenterZ=0 NormalX=0 NormalY=0 NormalZ=1 AngleXU=0 Radius=4
    g334: BSplineCurve PolesCount=3 KnotsCount=2 Degree=2 IsPeriodic=0
    g335: GeomPoint X=318.073 Y=72.4095 Z=0
    g336: GeomPoint X=322.073 Y=76.4095 Z=0
    g337: Circle CenterX=375.073 CenterY=72.4095 CenterZ=0 NormalX=0 NormalY=0 NormalZ=1 AngleXU=0 Radius=1
    g338: Circle CenterX=375.073 CenterY=76.4095 CenterZ=0 NormalX=0 NormalY=0 NormalZ=1 AngleXU=0 Radius=1
    g339: Circle CenterX=371.073 CenterY=76.4095 CenterZ=0 NormalX=0 NormalY=0 NormalZ=1 AngleXU=0 Radius=1
    g340: BSplineCurve PolesCount=3 KnotsCount=2 Degree=2 IsPeriodic=0
    g341: GeomPoint X=375.073 Y=72.4095 Z=0
    g342: GeomPoint X=371.073 Y=76.4095 Z=0
    g343: LineSegment StartX=322.073 StartY=76.4095 StartZ=0 EndX=371.073 EndY=76.4095 EndZ=0
    g344: LineSegment StartX=318.073 StartY=72.4095 StartZ=0 EndX=318.073 EndY=-47.4805 EndZ=0
    g345: LineSegment StartX=375.073 StartY=72.4095 StartZ=0 EndX=375.073 EndY=-78.7896 EndZ=0
    g346: ArcOfCircle CenterX=-26.9272 CenterY=22.1087 CenterZ=0 NormalX=0 NormalY=0 NormalZ=1 AngleXU=0 Radius=4 StartAngle=5e-16 EndAngle=3.14159
    g347: LineSegment StartX=-30.9272 StartY=22.1087 StartZ=0 EndX=-34.9272 EndY=-83.7794 EndZ=0
    g348: LineSegment StartX=-18.9272 StartY=-83.7794 StartZ=0 EndX=-22.9272 EndY=22.1087 EndZ=0
  constraints (572):
    c: Coincident(g0,g2)
    c: Block(g0)
    c: Block(g1)
    c: Vertical(g3)
    c: Vertical(g4)
    c: Block(g4)
    c: Block(g3)
    c: Tangent(g6,g7) = 1.5708
    c: Tangent(g7,g9) = 1.5708
    c: Equal(g6,g9)
    c: Coincident(g8,g6)
    c: Coincident(g8,g9)
    c: Block(g7)
    c: Block(g8)
    c: Weight(g10) = 1
    c: Equal(g10,g11)
    c: Equal(g10,g12)
    c: InternalAlignment(g10,g13)
    c: InternalAlignment(g11,g13)
    c: InternalAlignment(g12,g13)
    c: InternalAlignment(g14,g13)
    c: InternalAlignment(g15,g13)
    c: Weight(g16) = 1
    c: Equal(g16,g17)
    c: Equal(g16,g18)
    c: InternalAlignment(g16,g19)
    c: InternalAlignment(g17,g19)
    c: InternalAlignment(g18,g19)
    c: InternalAlignment(g20,g19)
    c: InternalAlignment(g21,g19)
    c: Block(g19)
    c: Block(g13)
    c: Weight(g22) = 1
    c: Equal(g22,g23)
    c: Equal(g22,g24)
    c: InternalAlignment(g22,g25)
    c: InternalAlignment(g23,g25)
    c: InternalAlignment(g24,g25)
    c: InternalAlignment(g26,g25)
    c: InternalAlignment(g27,g25)
    c: Weight(g28) = 1
    c: Equal(g28,g29)
    c: Equal(g28,g30)
    c: InternalAlignment(g28,g31)
    c: InternalAlignment(g29,g31)
    c: InternalAlignment(g30,g31)
    c: InternalAlignment(g32,g31)
    c: InternalAlignment(g33,g31)
    c: Block(g31)
    c: Block(g25)
    c: Weight(g34) = 1
    c: Equal(g34,g35)
    c: Equal(g34,g36)
    c: InternalAlignment(g34,g37)
    c: InternalAlignment(g35,g37)
    c: InternalAlignment(g36,g37)
    c: InternalAlignment(g38,g37)
    c: InternalAlignment(g39,g37)
    c: Weight(g40) = 1
    c: Equal(g40,g41)
    c: Equal(g40,g42)
    c: InternalAlignment(g40,g43)
    c: InternalAlignment(g41,g43)
    c: InternalAlignment(g42,g43)
    c: InternalAlignment(g44,g43)
    c: InternalAlignment(g45,g43)
    c: Block(g37)
    c: Block(g43)
    c: Coincident(g46,g4)
    c: Coincident(g46,g3)
    c: Horizontal(g46)
    c: Distance(g46) = 450
    c: Coincident(g47,g4)
    c: Coincident(g47,g3)
    c: Horizontal(g47)
    c: Horizontal(g48)
    c: Coincident(g2,g48)
    c: Block(g48)
    c: Coincident(g1,g48)
    c: Weight(g49) = 1
    c: Equal(g49,g50)
    c: Equal(g49,g51)
    c: InternalAlignment(g49,g52)
    c: InternalAlignment(g50,g52)
    c: InternalAlignment(g51,g52)
    c: InternalAlignment(g53,g52)
    c: InternalAlignment(g54,g52)
    c: Block(g52)
    c: Weight(g55) = 1
    c: Equal(g55,g56)
    c: Equal(g55,g57)
    c: InternalAlignment(g55,g58)
    c: InternalAlignment(g56,g58)
    c: InternalAlignment(g57,g58)
    c: InternalAlignment(g59,g58)
    c: InternalAlignment(g60,g58)
    c: Block(g58)
    c: Weight(g61) = 1
    c: Equal(g61,g62)
    c: Equal(g61,g63)
    c: InternalAlignment(g61,g64)
    c: InternalAlignment(g62,g64)
    c: InternalAlignment(g63,g64)
    c: InternalAlignment(g65,g64)
    c: InternalAlignment(g66,g64)
    c: Block(g64)
    c: Weight(g67) = 1
    c: Equal(g67,g68)
    c: Equal(g67,g69)
    c: InternalAlignment(g67,g70)
    c: InternalAlignment(g68,g70)
    c: InternalAlignment(g69,g70)
    c: InternalAlignment(g71,g70)
    c: InternalAlignment(g72,g70)
    c: Block(g70)
    c: Weight(g73) = 1
    c: Equal(g73,g74)
    c: Equal(g73,g75)
    c: InternalAlignment(g73,g76)
    c: InternalAlignment(g74,g76)
    c: InternalAlignment(g75,g76)
    c: InternalAlignment(g77,g76)
    c: InternalAlignment(g78,g76)
    c: Weight(g79) = 1
    c: Equal(g79,g80)
    c: Equal(g79,g81)
    c: InternalAlignment(g79,g82)
    c: InternalAlignment(g80,g82)
    c: InternalAlignment(g81,g82)
    c: InternalAlignment(g83,g82)
    c: InternalAlignment(g84,g82)
    c: Block(g76)
    c: Block(g82)
    c: Coincident(g85,g76)
    c: Coincident(g85,g82)
    c: Vertical(g85)
    c: Coincident(g86,g76)
    c: Coincident(g86,g58)
    c: Coincident(g87,g58)
    c: Coincident(g87,g82)
    c: Weight(g88) = 1
    c: Equal(g88,g89)
    c: Equal(g88,g90)
    c: InternalAlignment(g88,g91)
    c: InternalAlignment(g89,g91)
    c: InternalAlignment(g90,g91)
    c: InternalAlignment(g92,g91)
    c: InternalAlignment(g93,g91)
    c: Weight(g94) = 1
    c: Equal(g94,g95)
    c: Equal(g94,g96)
    c: InternalAlignment(g94,g97)
    c: InternalAlignment(g95,g97)
    c: InternalAlignment(g96,g97)
    c: InternalAlignment(g98,g97)
    c: InternalAlignment(g99,g97)
    c: Block(g91)
    c: Block(g97)
    c: Coincident(g100,g91)
    c: Coincident(g100,g97)
    c: Vertical(g100)
    c: Coincident(g101,g91)
    c: Coincident(g101,g52)
    c: Coincident(g102,g52)
    c: Coincident(g102,g97)
    c: Weight(g103) = 1
    c: Equal(g103,g104)
    c: Equal(g103,g105)
    c: InternalAlignment(g103,g106)
    c: InternalAlignment(g104,g106)
    c: InternalAlignment(g105,g106)
    c: InternalAlignment(g107,g106)
    c: InternalAlignment(g108,g106)
    c: Weight(g109) = 1
    c: Equal(g109,g110)
    c: Equal(g109,g111)
    c: InternalAlignment(g109,g112)
    c: InternalAlignment(g110,g112)
    c: InternalAlignment(g111,g112)
    c: InternalAlignment(g113,g112)
    c: InternalAlignment(g114,g112)
    c: Block(g106)
    c: Block(g112)
    c: Coincident(g115,g106)
    c: Coincident(g115,g112)
    c: Vertical(g115)
    c: Coincident(g116,g112)
    c: Coincident(g116,g70)
    c: Coincident(g117,g70)
    c: Coincident(g117,g106)
    c: Weight(g118) = 1
    c: Equal(g118,g119)
    c: Equal(g118,g120)
    c: InternalAlignment(g118,g121)
    c: InternalAlignment(g119,g121)
    c: InternalAlignment(g120,g121)
    c: InternalAlignment(g122,g121)
    c: InternalAlignment(g123,g121)
    c: Weight(g124) = 1
    c: Equal(g124,g125)
    c: Equal(g124,g126)
    c: InternalAlignment(g124,g127)
    c: InternalAlignment(g125,g127)
    c: InternalAlignment(g126,g127)
    c: InternalAlignment(g128,g127)
    c: InternalAlignment(g129,g127)
    c: Block(g121)
    c: Block(g127)
    c: Coincident(g130,g121)
    c: Coincident(g130,g127)
    c: Vertical(g130)
    c: Coincident(g131,g127)
    c: Coincident(g131,g64)
    c: Coincident(g132,g64)
    c: Coincident(g132,g121)
    c: Weight(g133) = 1
    c: Equal(g133,g134)
    c: Equal(g133,g135)
    c: InternalAlignment(g133,g136)
    c: InternalAlignment(g134,g136)
    c: InternalAlignment(g135,g136)
    c: InternalAlignment(g137,g136)
    c: InternalAlignment(g138,g136)
    c: Weight(g139) = 1
    c: Equal(g139,g140)
    c: Equal(g139,g141)
    c: InternalAlignment(g139,g142)
    c: InternalAlignment(g140,g142)
    c: InternalAlignment(g141,g142)
    c: InternalAlignment(g143,g142)
    c: InternalAlignment(g144,g142)
    c: Weight(g145) = 1
    c: Equal(g145,g146)
    c: Equal(g145,g147)
    c: InternalAlignment(g145,g148)
    c: InternalAlignment(g146,g148)
    c: InternalAlignment(g147,g148)
    c: InternalAlignment(g149,g148)
    c: InternalAlignment(g150,g148)
    c: Weight(g151) = 1
    c: Equal(g151,g152)
    c: Equal(g151,g153)
    c: InternalAlignment(g151,g154)
    c: InternalAlignment(g152,g154)
    c: InternalAlignment(g153,g154)
    c: InternalAlignment(g155,g154)
    c: InternalAlignment(g156,g154)
    c: Block(g154)
    c: Block(g148)
    c: Block(g142)
    c: Block(g136)
    c: Coincident(g157,g31)
    c: Coincident(g157,g154)
    c: Coincident(g158,g154)
    c: Coincident(g158,g148)
    c: Horizontal(g158)
    c: Coincident(g159,g148)
    c: Coincident(g159,g31)
    c: Vertical(g159)
    c: Coincident(g160,g25)
    c: Coincident(g160,g142)
    c: Vertical(g160)
    c: Coincident(g161,g142)
    c: Coincident(g161,g136)
    c: Horizontal(g161)
    c: Coincident(g162,g136)
    c: Coincident(g162,g25)
    c: Weight(g163) = 1
    c: Equal(g163,g164)
    c: Equal(g163,g165)
    c: InternalAlignment(g163,g166)
    c: InternalAlignment(g164,g166)
    c: InternalAlignment(g165,g166)
    c: InternalAlignment(g167,g166)
    c: InternalAlignment(g168,g166)
    c: Weight(g169) = 1
    c: Equal(g169,g170)
    c: Equal(g169,g171)
    c: InternalAlignment(g169,g172)
    c: InternalAlignment(g170,g172)
    c: InternalAlignment(g171,g172)
    c: InternalAlignment(g173,g172)
    c: InternalAlignment(g174,g172)
    c: Weight(g175) = 1
    c: Equal(g175,g176)
    c: Equal(g175,g177)
    c: InternalAlignment(g175,g178)
    c: InternalAlignment(g176,g178)
    c: InternalAlignment(g177,g178)
    c: InternalAlignment(g179,g178)
    c: InternalAlignment(g180,g178)
    c: Weight(g181) = 1
    c: Equal(g181,g182)
    c: Equal(g181,g183)
    c: InternalAlignment(g181,g184)
    c: InternalAlignment(g182,g184)
    c: InternalAlignment(g183,g184)
    c: InternalAlignment(g185,g184)
    c: InternalAlignment(g186,g184)
    c: Block(g184)
    c: Block(g178)
    c: Block(g172)
    c: Block(g166)
    c: Coincident(g187,g184)
    c: Coincident(g187,g178)
    c: Horizontal(g187)
    c: Coincident(g188,g178)
    c: Coincident(g188,g13)
    c: Vertical(g188)
    c: Coincident(g189,g19)
    c: Coincident(g189,g172)
    c: Vertical(g189)
    c: Coincident(g190,g172)
    c: Coincident(g190,g166)
    c: Horizontal(g190)
    c: Coincident(g191,g166)
    c: Coincident(g191,g19)
    c: Coincident(g192,g13)
    c: Weight(g193) = 1
    c: Equal(g193,g194)
    c: Equal(g193,g195)
    c: InternalAlignment(g193,g196)
    c: InternalAlignment(g194,g196)
    c: InternalAlignment(g195,g196)
    c: InternalAlignment(g197,g196)
    c: InternalAlignment(g198,g196)
    c: Weight(g199) = 1
    c: Equal(g199,g200)
    c: Equal(g199,g201)
    c: InternalAlignment(g199,g202)
    c: InternalAlignment(g200,g202)
    c: InternalAlignment(g201,g202)
    c: InternalAlignment(g203,g202)
    c: InternalAlignment(g204,g202)
    c: Block(g202)
    c: Block(g196)
    c: Coincident(g205,g202)
    c: Coincident(g205,g37)
    c: Coincident(g206,g37)
    c: Coincident(g206,g196)
    c: Coincident(g207,g196)
    c: Coincident(g207,g202)
    c: Vertical(g207)
    c: Weight(g208) = 1
    c: Equal(g208,g209)
    c: Equal(g208,g210)
    c: InternalAlignment(g208,g211)
    c: InternalAlignment(g209,g211)
    c: InternalAlignment(g210,g211)
    c: InternalAlignment(g212,g211)
    c: InternalAlignment(g213,g211)
    c: Weight(g214) = 1
    c: Equal(g214,g215)
    c: Equal(g214,g216)
    c: InternalAlignment(g214,g217)
    c: InternalAlignment(g215,g217)
    c: InternalAlignment(g216,g217)
    c: InternalAlignment(g218,g217)
    c: InternalAlignment(g219,g217)
    c: Block(g217)
    c: Block(g211)
    c: Coincident(g220,g211)
    c: Coincident(g220,g43)
    c: Coincident(g221,g43)
    c: Coincident(g221,g217)
    c: Coincident(g222,g217)
    c: Coincident(g222,g211)
    c: Vertical(g222)
    c: Horizontal(g223)
    c: Block(g223)
    c: Vertical(g224)
    c: Block(g224)
    c: Block(g225)
    c: Weight(g226) = 1
    c: Equal(g226,g227)
    c: Equal(g226,g228)
    c: InternalAlignment(g226,g229)
    c: InternalAlignment(g227,g229)
    c: InternalAlignment(g228,g229)
    c: InternalAlignment(g230,g229)
    c: InternalAlignment(g231,g229)
    c: Weight(g232) = 1
    c: Equal(g232,g233)
    c: Equal(g232,g234)
    c: InternalAlignment(g232,g235)
    c: InternalAlignment(g233,g235)
    c: InternalAlignment(g234,g235)
    c: InternalAlignment(g236,g235)
    c: InternalAlignment(g237,g235)
    c: Weight(g238) = 1
    c: Equal(g238,g239)
    c: Equal(g238,g240)
    c: InternalAlignment(g238,g241)
    c: InternalAlignment(g239,g241)
    c: InternalAlignment(g240,g241)
    c: InternalAlignment(g242,g241)
    c: InternalAlignment(g243,g241)
    c: Weight(g244) = 1
    c: Equal(g244,g245)
    c: Equal(g244,g246)
    c: InternalAlignment(g244,g247)
    c: InternalAlignment(g245,g247)
    c: InternalAlignment(g246,g247)
    c: InternalAlignment(g248,g247)
    c: InternalAlignment(g249,g247)
    c: Block(g229)
    c: Block(g235)
    c: Block(g241)
    c: Block(g247)
    c: Coincident(g250,g235)
    c: Coincident(g250,g229)
    c: Horizontal(g250)
    c: Block(g192)
    c: Weight(g251) = 1
    c: Equal(g251,g252)
    c: Equal(g251,g253)
    c: InternalAlignment(g251,g254)
    c: InternalAlignment(g252,g254)
    c: InternalAlignment(g253,g254)
    c: InternalAlignment(g255,g254)
    c: InternalAlignment(g256,g254)
    c: Weight(g257) = 1
    c: Equal(g257,g258)
    c: Equal(g257,g259)
    c: InternalAlignment(g257,g260)
    c: InternalAlignment(g258,g260)
    c: InternalAlignment(g259,g260)
    c: InternalAlignment(g261,g260)
    c: InternalAlignment(g262,g260)
    c: Block(g254)
    c: Block(g260)
    c: Coincident(g263,g254)
    c: Coincident(g263,g260)
    c: Weight(g264) = 1
    c: Equal(g264,g265)
    c: Equal(g264,g266)
    c: InternalAlignment(g264,g267)
    c: InternalAlignment(g265,g267)
    c: InternalAlignment(g266,g267)
    c: InternalAlignment(g268,g267)
    c: InternalAlignment(g269,g267)
    c: Weight(g270) = 1
    c: Equal(g270,g271)
    c: Equal(g270,g272)
    c: InternalAlignment(g270,g273)
    c: InternalAlignment(g271,g273)
    c: InternalAlignment(g272,g273)
    c: InternalAlignment(g274,g273)
    c: InternalAlignment(g275,g273)
    c: Weight(g276) = 1
    c: Equal(g276,g277)
    c: Equal(g276,g278)
    c: InternalAlignment(g276,g279)
    c: InternalAlignment(g277,g279)
    c: InternalAlignment(g278,g279)
    c: InternalAlignment(g280,g279)
    c: InternalAlignment(g281,g279)
    c: Block(g279)
    c: Block(g273)
    c: Block(g267)
    c: Coincident(g282,g273)
    c: Coincident(g282,g267)
    c: Coincident(g283,g267)
    c: Coincident(g283,g279)
    c: Vertical(g283)
    c: Coincident(g284,g279)
    c: Coincident(g284,g273)
    c: Horizontal(g284)
    c: Weight(g285) = 1
    c: Equal(g285,g286)
    c: InternalAlignment(g285,g287)
    c: InternalAlignment(g286,g287)
    c: InternalAlignment(g288,g287)
    c: InternalAlignment(g289,g287)
    c: Weight(g290) = 1
    c: InternalAlignment(g291,g293)
    c: InternalAlignment(g292,g293)
    c: InternalAlignment(g294,g293)
    c: InternalAlignment(g295,g293)
    c: Weight(g296) = 1
    c: Equal(g296,g297)
    c: Equal(g296,g298)
    c: InternalAlignment(g296,g299)
    c: InternalAlignment(g297,g299)
    c: InternalAlignment(g298,g299)
    c: InternalAlignment(g300,g299)
    c: InternalAlignment(g301,g299)
    c: Equal(g302,g303)
    c: Equal(g302,g304)
    c: InternalAlignment(g302,g305)
    c: InternalAlignment(g303,g305)
    c: InternalAlignment(g304,g305)
    c: InternalAlignment(g306,g305)
    c: InternalAlignment(g307,g305)
    c: Block(g293)
    c: Block(g299)
    c: Block(g305)
    c: Block(g287)
    c: Coincident(g308,g287)
    c: Coincident(g308,g293)
    c: Horizontal(g308)
    c: Coincident(g309,g293)
    c: Coincident(g309,g299)
    c: Vertical(g309)
    c: Coincident(g310,g299)
    c: Coincident(g310,g305)
    c: Horizontal(g310)
    c: Coincident(g311,g305)
    c: Coincident(g311,g287)
    c: Weight(g312) = 1
    c: Equal(g312,g313)
    c: Equal(g312,g314)
    c: InternalAlignment(g312,g315)
    c: InternalAlignment(g313,g315)
    c: InternalAlignment(g314,g315)
    c: InternalAlignment(g316,g315)
    c: InternalAlignment(g317,g315)
    c: Weight(g318) = 1
    c: Equal(g318,g319)
    c: Equal(g318,g320)
    c: InternalAlignment(g318,g321)
    c: InternalAlignment(g319,g321)
    c: InternalAlignment(g320,g321)
    c: InternalAlignment(g322,g321)
    c: InternalAlignment(g323,g321)
    c: Weight(g324) = 1
    c: Equal(g324,g325)
    c: Equal(g324,g326)
    c: InternalAlignment(g324,g327)
    c: InternalAlignment(g325,g327)
    c: InternalAlignment(g326,g327)
    c: InternalAlignment(g328,g327)
    c: InternalAlignment(g329,g327)
    c: Block(g327)
    c: Block(g321)
    c: Block(g315)
    c: Coincident(g330,g327)
    c: Coincident(g330,g321)
    c: Horizontal(g330)
    c: Coincident(g331,g321)
    c: Coincident(g331,g315)
    c: Vertical(g331)
    c: Coincident(g332,g315)
    c: Coincident(g332,g327)
    c: InternalAlignment(g333,g334)
    c: InternalAlignment(g335,g334)
    c: InternalAlignment(g336,g334)
    c: Block(g334)
    c: Equal(g337,g338)
    c: Equal(g337,g339)
    c: InternalAlignment(g337,g340)
    c: InternalAlignment(g338,g340)
    c: InternalAlignment(g339,g340)
    c: InternalAlignment(g341,g340)
    c: InternalAlignment(g342,g340)
    c: Block(g340)
    c: Coincident(g343,g334)
    c: Horizontal(g343)
    c: Block(g343)
    c: Coincident(g344,g334)
    c: Coincident(g344,g260)
    c: Vertical(g344)
    c: Coincident(g345,g340)
    c: Coincident(g345,g254)
    c: Vertical(g345)
    c: Coincident(g347,g5)
    c: Coincident(g348,g5)
    c: Block(g346)
    c: Block(g5)
    c: Block(g348)
    c: Block(g347)
    c: Distance(g344) = 119.89
FEATURE [Sketcher::SketchObject] Sketch001
  FullyConstrained = true
  MapMode = 4
  Placement = pos=(0,0,0) rot=(0.57735,0.57735,0.57735;2.0944rad)
  Support = -> [Sketch]
  sketch-geometry (46):
    g0: BSplineCurve PolesCount=3 KnotsCount=2 Degree=2 IsPeriodic=0
    g1: ArcOfCircle CenterX=73.1223 CenterY=-32.291 CenterZ=0 NormalX=0 NormalY=0 NormalZ=1 AngleXU=0 Radius=13 StartAngle=5.92268 EndAngle=9.06428
    g2: ArcOfCircle CenterX=66.7816 CenterY=-49.1439 CenterZ=0 NormalX=0 NormalY=0 NormalZ=1 AngleXU=0 Radius=13 StartAngle=2.78068 EndAngle=5.92131
    g3: ArcOfCircle CenterX=55.9263 CenterY=-78.1807 CenterZ=0 NormalX=0 NormalY=0 NormalZ=1 AngleXU=0 Radius=13 StartAngle=5.92268 EndAngle=9.06428
    g4: ArcOfCircle CenterX=49.5884 CenterY=-95.0342 CenterZ=0 NormalX=0 NormalY=0 NormalZ=1 AngleXU=0 Radius=13 StartAngle=2.78068 EndAngle=5.92131
    g5: ArcOfCircle CenterX=38.7206 CenterY=-124.067 CenterZ=0 NormalX=0 NormalY=0 NormalZ=1 AngleXU=0 Radius=13 StartAngle=5.92268 EndAngle=9.06428
    g6: ArcOfCircle CenterX=32.3875 CenterY=-140.92 CenterZ=0 NormalX=0 NormalY=0 NormalZ=1 AngleXU=0 Radius=13 StartAngle=2.78068 EndAngle=5.92131
    g7: ArcOfCircle CenterX=21.4715 CenterY=-169.934 CenterZ=0 NormalX=0 NormalY=0 NormalZ=1 AngleXU=0 Radius=13 StartAngle=5.92268 EndAngle=9.06428
    g8: ArcOfCircle CenterX=15.1336 CenterY=-186.787 CenterZ=0 NormalX=0 NormalY=0 NormalZ=1 AngleXU=0 Radius=13 StartAngle=2.78068 EndAngle=5.92131
    g9-g12: Circle x4 (B-spline internal-alignment scaffolding for g13; pole/knot coordinates omitted)
    g13: BSplineCurve PolesCount=4 KnotsCount=2 Degree=3 IsPeriodic=0
    g14: GeomPoint X=28.8094 Y=-19.0875 Z=0
    g15: GeomPoint X=47.0443 Y=-50.4712 Z=0
    g16: Circle CenterX=53.5586 CenterY=-23.2695 CenterZ=0 NormalX=0 NormalY=0 NormalZ=1 AngleXU=0 Radius=3.24518
    g17: Circle CenterX=-195.441 CenterY=-127.082 CenterZ=0 NormalX=0 NormalY=0 NormalZ=1 AngleXU=0 Radius=1
    g18: Circle CenterX=-8.24091 CenterY=-197.481 CenterZ=0 NormalX=0 NormalY=0 NormalZ=1 AngleXU=0 Radius=1
    g19: Circle CenterX=12.8789 CenterY=-141.321 CenterZ=0 NormalX=0 NormalY=0 NormalZ=1 AngleXU=0 Radius=1
    g20: BSplineCurve PolesCount=3 KnotsCount=2 Degree=2 IsPeriodic=0
    g21: GeomPoint X=-195.441 Y=-127.082 Z=0
    g22: GeomPoint X=12.8789 Y=-141.321 Z=0
    g23: Circle CenterX=-12.8016 CenterY=-179.036 CenterZ=0 NormalX=0 NormalY=0 NormalZ=1 AngleXU=0 Radius=10.5072
    g24: Circle CenterX=0.933922 CenterY=-166.43 CenterZ=0 NormalX=0 NormalY=0 NormalZ=1 AngleXU=0 Radius=3.26661
    g25: Circle CenterX=-33.5518 CenterY=-176.44 CenterZ=0 NormalX=0 NormalY=0 NormalZ=1 AngleXU=0 Radius=5.64388
    g26: Circle CenterX=-47.2366 CenterY=-173.859 CenterZ=0 NormalX=0 NormalY=0 NormalZ=1 AngleXU=0 Radius=3.01653
    g27: Circle CenterX=-56.2595 CenterY=-171.456 CenterZ=0 NormalX=0 NormalY=0 NormalZ=1 AngleXU=0 Radius=2.12826
    g28: ArcOfCircle CenterX=51.2151 CenterY=-198.473 CenterZ=0 NormalX=0 NormalY=0 NormalZ=1 AngleXU=0 Radius=20 StartAngle=2.78189 EndAngle=4.35269
    g29: LineSegment StartX=32.4951 StartY=-191.433 StartZ=0 EndX=94.6578 EndY=-26.1352 EndZ=0
    g30: LineSegment StartX=43.1192 StartY=-220.001 StartZ=0 EndX=-196.497 EndY=-129.89 EndZ=0
    g31: LineSegment StartX=43.1192 StartY=-220.001 StartZ=0 EndX=44.1752 EndY=-217.193 EndZ=0
    g32: LineSegment StartX=117.223 StartY=-19.0875 StartZ=0 EndX=117.223 EndY=-16.0875 EndZ=0
    g33: LineSegment StartX=117.223 StartY=-16.0875 StartZ=0 EndX=17.2232 EndY=-16.0875 EndZ=0
    g34: LineSegment StartX=17.2232 StartY=-16.0875 StartZ=0 EndX=17.2232 EndY=-19.0875 EndZ=0
    g35: LineSegment StartX=28.8094 StartY=-19.0875 StartZ=0 EndX=17.2232 EndY=-19.0875 EndZ=0
    g36: LineSegment StartX=47.0443 StartY=-50.4712 StartZ=0 EndX=12.8789 EndY=-141.321 EndZ=0
    g37: LineSegment StartX=-195.441 StartY=-127.082 StartZ=0 EndX=-196.497 EndY=-129.89 EndZ=0
    g38: LineSegment StartX=85.2866 StartY=-36.8766 StartZ=0 EndX=78.9396 EndY=-53.7463 EndZ=0
    g39: LineSegment StartX=60.9579 StartY=-27.7053 StartZ=0 EndX=54.6191 EndY=-44.5532 EndZ=0
    g40: LineSegment StartX=68.0907 StartY=-82.7664 StartZ=0 EndX=61.7465 EndY=-99.6365 EndZ=0
    g41: LineSegment StartX=43.7619 StartY=-73.595 StartZ=0 EndX=37.426 EndY=-90.4435 EndZ=0
    g42: LineSegment StartX=50.885 StartY=-128.652 StartZ=0 EndX=44.5456 EndY=-145.522 EndZ=0
    g43: LineSegment StartX=26.5562 StartY=-119.481 StartZ=0 EndX=20.2251 EndY=-136.329 EndZ=0
    g44: LineSegment StartX=9.3071 StartY=-165.349 StartZ=0 EndX=2.97115 EndY=-182.197 EndZ=0
    g45: LineSegment StartX=33.6358 StartY=-174.52 StartZ=0 EndX=27.2917 EndY=-191.39 EndZ=0
  constraints (71):
    c: Block(g0)
    c: Block(g1)
    c: Block(g2)
    c: Block(g4)
    c: Block(g3)
    c: Block(g6)
    c: Block(g5)
    c: Block(g8)
    c: Block(g7)
    c: Weight(g9) = 1
    c: Equal(g9,g10)
    c: Equal(g9,g11)
    c: Equal(g9,g12)
    c: InternalAlignment(g9-g12 -> g13) x4
    c: InternalAlignment(g14,g13)
    c: InternalAlignment(g15,g13)
    c: Block(g16)
    c: Weight(g17) = 1
    c: Equal(g17,g18)
    c: Equal(g17,g19)
    c: InternalAlignment(g17,g20)
    c: InternalAlignment(g18,g20)
    c: InternalAlignment(g19,g20)
    c: InternalAlignment(g21,g20)
    c: InternalAlignment(g22,g20)
    c: Block(g20)
    c: Block(g23)
    c: Block(g24)
    c: Block(g25)
    c: Block(g26)
    c: Block(g27)
    c: Block(g28)
    c: Coincident(g29,g28)
    c: Coincident(g29,g0)
    c: Block(g13)
    c: Coincident(g31,g30)
    c: Coincident(g31,g28)
    c: Block(g31)
    c: Coincident(g32,g0)
    c: Vertical(g32)
    c: Coincident(g33,g32)
    c: Horizontal(g33)
    c: Coincident(g34,g33)
    c: Vertical(g34)
    c: Block(g33)
    c: Coincident(g35,g13)
    c: Coincident(g35,g34)
    c: Horizontal(g35)
    c: Coincident(g36,g13)
    c: Coincident(g36,g20)
    c: Coincident(g37,g20)
    c: Coincident(g37,g30)
    c: Block(g30)
    c: Coincident(g38,g1)
    c: Coincident(g38,g2)
    c: Coincident(g39,g1)
    c: Coincident(g39,g2)
    c: Coincident(g40,g3)
    c: Coincident(g40,g4)
    c: Coincident(g41,g3)
    c: Coincident(g41,g4)
    c: Coincident(g42,g5)
    c: Coincident(g42,g6)
    c: Coincident(g43,g5)
    c: Coincident(g43,g6)
    c: Coincident(g44,g7)
    c: Coincident(g44,g8)
    c: Coincident(g45,g7)
    c: Coincident(g45,g8)
    c: Distance(g30) = 256
    c: Distance(g33) = 100
FEATURE [Part::Extrusion] Extrude002
  Base = -> Sketch001
  Dir = (1,0,0)
  DirMode = 2
  FaceMakerClass = Part::FaceMakerBullseye
  LengthFwd = 8
  LengthRev = 0
  Solid = true
  Symmetric = false
FEATURE [Sketcher::SketchObject] Sketch002
  FullyConstrained = true
  sketch-geometry (20):
    g0: LineSegment StartX=-2.77179 StartY=-200.304 StartZ=0 EndX=5.22821 EndY=-200.304 EndZ=0
    g1: LineSegment StartX=5.22821 StartY=-200.304 StartZ=0 EndX=5.22821 EndY=-197.304 EndZ=0
    g2: LineSegment StartX=-2.77179 StartY=-200.304 StartZ=0 EndX=-2.77179 EndY=-197.304 EndZ=0
    g3: LineSegment StartX=5.22821 StartY=-197.304 StartZ=0 EndX=8.22821 EndY=-197.304 EndZ=0
    g4: LineSegment StartX=-2.77179 StartY=-197.304 StartZ=0 EndX=-5.77179 EndY=-197.304 EndZ=0
    g5: LineSegment StartX=19.2282 StartY=-203.304 StartZ=0 EndX=19.2282 EndY=-206.304 EndZ=0
    g6: LineSegment StartX=-16.7718 StartY=-203.304 StartZ=0 EndX=-16.7718 EndY=-206.304 EndZ=0
    g7: LineSegment StartX=-16.7718 StartY=-206.304 StartZ=0 EndX=19.2282 EndY=-206.304 EndZ=0
    g8: Circle CenterX=-16.7718 CenterY=-203.304 CenterZ=0 NormalX=0 NormalY=0 NormalZ=1 AngleXU=0 Radius=1
    g9: Circle CenterX=-5.77179 CenterY=-203.304 CenterZ=0 NormalX=0 NormalY=0 NormalZ=1 AngleXU=0 Radius=1
    g10: Circle CenterX=-5.77179 CenterY=-197.304 CenterZ=0 NormalX=0 NormalY=0 NormalZ=1 AngleXU=0 Radius=1
    g11: BSplineCurve PolesCount=3 KnotsCount=2 Degree=2 IsPeriodic=0
    g12: GeomPoint X=-16.7718 Y=-203.304 Z=0
    g13: GeomPoint X=-5.77179 Y=-197.304 Z=0
    g14: Circle CenterX=19.2282 CenterY=-203.304 CenterZ=0 NormalX=0 NormalY=0 NormalZ=1 AngleXU=0 Radius=1
    g15: Circle CenterX=8.22821 CenterY=-203.304 CenterZ=0 NormalX=0 NormalY=0 NormalZ=1 AngleXU=0 Radius=1
    g16: Circle CenterX=8.22821 CenterY=-197.304 CenterZ=0 NormalX=0 NormalY=0 NormalZ=1 AngleXU=0 Radius=1
    g17: BSplineCurve PolesCount=3 KnotsCount=2 Degree=2 IsPeriodic=0
    g18: GeomPoint X=19.2282 Y=-203.304 Z=0
    g19: GeomPoint X=8.22821 Y=-197.304 Z=0
  constraints (41):
    c: Horizontal(g0)
    c: Distance(g0) = 8
    c: Coincident(g1,g0)
    c: Vertical(g1)
    c: Distance(g1) = 3
    c: Coincident(g2,g0)
    c: Vertical(g2)
    c: Distance(g2) = 3
    c: Coincident(g3,g1)
    c: Horizontal(g3)
    c: Distance(g3) = 3
    c: Coincident(g4,g2)
    c: Horizontal(g4)
    c: Distance(g4) = 3
    c: Vertical(g5)
    c: Vertical(g6)
    c: Coincident(g7,g6)
    c: Coincident(g7,g5)
    c: Weight(g8) = 1
    c: Equal(g8,g9)
    c: Equal(g8,g10)
    c: Coincident(g11,g4)
    c: InternalAlignment(g8,g11)
    c: InternalAlignment(g9,g11)
    c: InternalAlignment(g10,g11)
    c: InternalAlignment(g12,g11)
    c: InternalAlignment(g13,g11)
    c: Coincident(g17,g5)
    c: Weight(g14) = 1
    c: Equal(g14,g15)
    c: Equal(g14,g16)
    c: Coincident(g17,g3)
    c: InternalAlignment(g14,g17)
    c: InternalAlignment(g15,g17)
    c: InternalAlignment(g16,g17)
    c: InternalAlignment(g18,g17)
    c: InternalAlignment(g19,g17)
    c: Block(g7)
    c: Block(g17)
    c: Block(g11)
    c: Block(g6)
FEATURE [Part::Extrusion] Extrude003
  Base = -> Sketch002
  Dir = (0,0,1)
  DirMode = 2
  FaceMakerClass = Part::FaceMakerBullseye
  LengthFwd = 260
  LengthRev = 0
  Solid = true
  Symmetric = false
FEATURE [Part::Extrusion] Extrude
  Base = -> Sketch
  Dir = (0,0,1)
  DirMode = 2
  FaceMakerClass = Part::FaceMakerBullseye
  LengthFwd = 14
  LengthRev = 0
  Solid = true
  Symmetric = false
FEATURE [Sketcher::SketchObject] Sketch003
  FullyConstrained = false
  sketch-geometry (349):
    g0: LineSegment StartX=-10.9272 StartY=-82.7794 StartZ=0 EndX=46.0728 EndY=-51.4823 EndZ=0
    g1: LineSegment StartX=-10.9272 StartY=76.4095 StartZ=0 EndX=-10.9272 EndY=-82.7794 EndZ=0
    g2: LineSegment StartX=46.0728 StartY=76.4095 StartZ=0 EndX=46.0728 EndY=-51.4823 EndZ=0
    g3: LineSegment StartX=-42.9272 StartY=136.221 StartZ=0 EndX=-42.9272 EndY=-103.779 EndZ=0
    g4: LineSegment StartX=407.073 StartY=136.221 StartZ=0 EndX=407.073 EndY=-103.779 EndZ=0
    g5: ArcOfCircle CenterX=-26.9272 CenterY=-83.7794 CenterZ=0 NormalX=0 NormalY=0 NormalZ=1 AngleXU=0 Radius=8 StartAngle=3.14159 EndAngle=6.28319
    g6: ArcOfCircle CenterX=391.073 CenterY=22.1087 CenterZ=0 NormalX=0 NormalY=0 NormalZ=1 AngleXU=0 Radius=8 StartAngle=-4.4e-15 EndAngle=3.14159
    g7: LineSegment StartX=399.073 StartY=22.1087 StartZ=0 EndX=399.073 EndY=-83.7794 EndZ=0
    g8: LineSegment StartX=383.073 StartY=22.1087 StartZ=0 EndX=383.073 EndY=-83.7794 EndZ=0
    g9: ArcOfCircle CenterX=391.073 CenterY=-83.7794 CenterZ=0 NormalX=0 NormalY=0 NormalZ=1 AngleXU=0 Radius=8 StartAngle=3.14159 EndAngle=6.28319
    g10: Circle CenterX=175.022 CenterY=27.0628 CenterZ=0 NormalX=0 NormalY=0 NormalZ=1 AngleXU=0 Radius=1
    g11: Circle CenterX=179.022 CenterY=24.8665 CenterZ=0 NormalX=0 NormalY=0 NormalZ=1 AngleXU=0 Radius=1
    g12: Circle CenterX=179.022 CenterY=27.0628 CenterZ=0 NormalX=0 NormalY=0 NormalZ=1 AngleXU=0 Radius=1
    g13: BSplineCurve PolesCount=3 KnotsCount=2 Degree=2 IsPeriodic=0
    g14: GeomPoint X=175.022 Y=27.0628 Z=0
    g15: GeomPoint X=179.022 Y=27.0628 Z=0
    g16: Circle CenterX=189.124 CenterY=27.0628 CenterZ=0 NormalX=0 NormalY=0 NormalZ=1 AngleXU=0 Radius=1
    g17: Circle CenterX=185.124 CenterY=24.8665 CenterZ=0 NormalX=0 NormalY=0 NormalZ=1 AngleXU=0 Radius=1
    g18: Circle CenterX=185.124 CenterY=27.0628 CenterZ=0 NormalX=0 NormalY=0 NormalZ=1 AngleXU=0 Radius=1
    g19: BSplineCurve PolesCount=3 KnotsCount=2 Degree=2 IsPeriodic=0
    g20: GeomPoint X=189.124 Y=27.0628 Z=0
    g21: GeomPoint X=185.124 Y=27.0628 Z=0
    g22: Circle CenterX=175.022 CenterY=5.37834 CenterZ=0 NormalX=0 NormalY=0 NormalZ=1 AngleXU=0 Radius=1
    g23: Circle CenterX=179.022 CenterY=7.57463 CenterZ=0 NormalX=0 NormalY=0 NormalZ=1 AngleXU=0 Radius=1
    g24: Circle CenterX=179.022 CenterY=5.34704 CenterZ=0 NormalX=0 NormalY=0 NormalZ=1 AngleXU=0 Radius=1
    g25: BSplineCurve PolesCount=3 KnotsCount=2 Degree=2 IsPeriodic=0
    g26: GeomPoint X=175.022 Y=5.37834 Z=0
    g27: GeomPoint X=179.022 Y=5.34704 Z=0
    g28: Circle CenterX=189.124 CenterY=5.37834 CenterZ=0 NormalX=0 NormalY=0 NormalZ=1 AngleXU=0 Radius=1
    g29: Circle CenterX=185.124 CenterY=7.57463 CenterZ=0 NormalX=0 NormalY=0 NormalZ=1 AngleXU=0 Radius=1
    g30: Circle CenterX=185.124 CenterY=5.34704 CenterZ=0 NormalX=0 NormalY=0 NormalZ=1 AngleXU=0 Radius=1
    g31: BSplineCurve PolesCount=3 KnotsCount=2 Degree=2 IsPeriodic=0
    g32: GeomPoint X=189.124 Y=5.37834 Z=0
    g33: GeomPoint X=185.124 Y=5.34704 Z=0
    g34: Circle CenterX=165.871 CenterY=18.1458 CenterZ=0 NormalX=0 NormalY=0 NormalZ=1 AngleXU=0 Radius=1
    g35: Circle CenterX=169.377 CenterY=16.2206 CenterZ=0 NormalX=0 NormalY=0 NormalZ=1 AngleXU=0 Radius=1
    g36: Circle CenterX=165.871 CenterY=14.2954 CenterZ=0 NormalX=0 NormalY=0 NormalZ=1 AngleXU=0 Radius=1
    g37: BSplineCurve PolesCount=3 KnotsCount=2 Degree=2 IsPeriodic=0
    g38: GeomPoint X=165.871 Y=18.1458 Z=0
    g39: GeomPoint X=165.871 Y=14.2954 Z=0
    g40: Circle CenterX=198.275 CenterY=18.1458 CenterZ=0 NormalX=0 NormalY=0 NormalZ=1 AngleXU=0 Radius=1
    g41: Circle CenterX=194.768 CenterY=16.2206 CenterZ=0 NormalX=0 NormalY=0 NormalZ=1 AngleXU=0 Radius=1
    g42: Circle CenterX=198.275 CenterY=14.2954 CenterZ=0 NormalX=0 NormalY=0 NormalZ=1 AngleXU=0 Radius=1
    g43: BSplineCurve PolesCount=3 KnotsCount=2 Degree=2 IsPeriodic=0
    g44: GeomPoint X=198.275 Y=18.1458 Z=0
    g45: GeomPoint X=198.275 Y=14.2954 Z=0
    g46: LineSegment StartX=407.073 StartY=-103.779 StartZ=0 EndX=-42.9272 EndY=-103.779 EndZ=0
    g47: LineSegment StartX=407.073 StartY=136.221 StartZ=0 EndX=-42.9272 EndY=136.221 EndZ=0
    g48: LineSegment StartX=46.0728 StartY=76.4095 StartZ=0 EndX=-10.9272 EndY=76.4095 EndZ=0
    g49: Circle CenterX=125.607 CenterY=54.1951 CenterZ=0 NormalX=0 NormalY=0 NormalZ=1 AngleXU=0 Radius=1
    g50: Circle CenterX=139.632 CenterY=46.4944 CenterZ=0 NormalX=0 NormalY=0 NormalZ=1 AngleXU=0 Radius=1
    g51: Circle CenterX=127.326 CenterY=56.7187 CenterZ=0 NormalX=0 NormalY=0 NormalZ=1 AngleXU=0 Radius=1
    g52: BSplineCurve PolesCount=3 KnotsCount=2 Degree=2 IsPeriodic=0
    g53: GeomPoint X=125.607 Y=54.1951 Z=0
    g54: GeomPoint X=127.326 Y=56.7187 Z=0
    g55: Circle CenterX=236.821 CenterY=56.7187 CenterZ=0 NormalX=0 NormalY=0 NormalZ=1 AngleXU=0 Radius=1
    g56: Circle CenterX=224.513 CenterY=46.4944 CenterZ=0 NormalX=0 NormalY=0 NormalZ=1 AngleXU=0 Radius=1
    g57: Circle CenterX=238.538 CenterY=54.1951 CenterZ=0 NormalX=0 NormalY=0 NormalZ=1 AngleXU=0 Radius=1
    g58: BSplineCurve PolesCount=3 KnotsCount=2 Degree=2 IsPeriodic=0
    g59: GeomPoint X=236.821 Y=56.7187 Z=0
    g60: GeomPoint X=238.538 Y=54.1951 Z=0
    g61: Circle CenterX=238.538 CenterY=-21.7539 CenterZ=0 NormalX=0 NormalY=0 NormalZ=1 AngleXU=0 Radius=1
    g62: Circle CenterX=224.513 CenterY=-14.0532 CenterZ=0 NormalX=0 NormalY=0 NormalZ=1 AngleXU=0 Radius=1
    g63: Circle CenterX=236.821 CenterY=-24.2775 CenterZ=0 NormalX=0 NormalY=0 NormalZ=1 AngleXU=0 Radius=1
    g64: BSplineCurve PolesCount=3 KnotsCount=2 Degree=2 IsPeriodic=0
    g65: GeomPoint X=238.538 Y=-21.7539 Z=0
    g66: GeomPoint X=236.821 Y=-24.2775 Z=0
    g67: Circle CenterX=125.607 CenterY=-21.7539 CenterZ=0 NormalX=0 NormalY=0 NormalZ=1 AngleXU=0 Radius=1
    g68: Circle CenterX=139.632 CenterY=-14.0532 CenterZ=0 NormalX=0 NormalY=0 NormalZ=1 AngleXU=0 Radius=1
    g69: Circle CenterX=127.325 CenterY=-24.2775 CenterZ=0 NormalX=0 NormalY=0 NormalZ=1 AngleXU=0 Radius=1
    g70: BSplineCurve PolesCount=3 KnotsCount=2 Degree=2 IsPeriodic=0
    g71: GeomPoint X=125.607 Y=-21.7539 Z=0
    g72: GeomPoint X=127.325 Y=-24.2775 Z=0
    g73: Circle CenterX=302.996 CenterY=111.695 CenterZ=0 NormalX=0 NormalY=0 NormalZ=1 AngleXU=0 Radius=1
    g74: Circle CenterX=306.073 CenterY=114.251 CenterZ=0 NormalX=0 NormalY=0 NormalZ=1 AngleXU=0 Radius=1
    g75: Circle CenterX=306.073 CenterY=110.251 CenterZ=0 NormalX=0 NormalY=0 NormalZ=1 AngleXU=0 Radius=1
    g76: BSplineCurve PolesCount=3 KnotsCount=2 Degree=2 IsPeriodic=0
    g77: GeomPoint X=302.996 Y=111.695 Z=0
    g78: GeomPoint X=306.073 Y=110.251 Z=0
    g79: Circle CenterX=306.073 CenterY=95.2763 CenterZ=0 NormalX=0 NormalY=0 NormalZ=1 AngleXU=0 Radius=1
    g80: Circle CenterX=306.073 CenterY=91.2763 CenterZ=0 NormalX=0 NormalY=0 NormalZ=1 AngleXU=0 Radius=1
    g81: Circle CenterX=302.567 CenterY=89.3511 CenterZ=0 NormalX=0 NormalY=0 NormalZ=1 AngleXU=0 Radius=1
    g82: BSplineCurve PolesCount=3 KnotsCount=2 Degree=2 IsPeriodic=0
    g83: GeomPoint X=306.073 Y=95.2763 Z=0
    g84: GeomPoint X=302.567 Y=89.3511 Z=0
    g85: LineSegment StartX=306.073 StartY=110.251 StartZ=0 EndX=306.073 EndY=95.2763 EndZ=0
    g86: LineSegment StartX=302.996 StartY=111.695 StartZ=0 EndX=236.821 EndY=56.7187 EndZ=0
    g87: LineSegment StartX=238.538 StartY=54.1951 StartZ=0 EndX=302.567 EndY=89.3511 EndZ=0
    g88: Circle CenterX=61.1496 CenterY=111.695 CenterZ=0 NormalX=0 NormalY=0 NormalZ=1 AngleXU=0 Radius=1
    g89: Circle CenterX=58.0728 CenterY=114.251 CenterZ=0 NormalX=0 NormalY=0 NormalZ=1 AngleXU=0 Radius=1
    g90: Circle CenterX=58.0728 CenterY=110.251 CenterZ=0 NormalX=0 NormalY=0 NormalZ=1 AngleXU=0 Radius=1
    g91: BSplineCurve PolesCount=3 KnotsCount=2 Degree=2 IsPeriodic=0
    g92: GeomPoint X=61.1496 Y=111.695 Z=0
    g93: GeomPoint X=58.0728 Y=110.251 Z=0
    g94: Circle CenterX=61.5791 CenterY=89.3511 CenterZ=0 NormalX=0 NormalY=0 NormalZ=1 AngleXU=0 Radius=1
    g95: Circle CenterX=58.0728 CenterY=91.2763 CenterZ=0 NormalX=0 NormalY=0 NormalZ=1 AngleXU=0 Radius=1
    g96: Circle CenterX=58.0728 CenterY=95.2763 CenterZ=0 NormalX=0 NormalY=0 NormalZ=1 AngleXU=0 Radius=1
    g97: BSplineCurve PolesCount=3 KnotsCount=2 Degree=2 IsPeriodic=0
    g98: GeomPoint X=61.5791 Y=89.3511 Z=0
    g99: GeomPoint X=58.0728 Y=95.2763 Z=0
    g100: LineSegment StartX=58.0728 StartY=110.251 StartZ=0 EndX=58.0728 EndY=95.2763 EndZ=0
    g101: LineSegment StartX=61.1496 StartY=111.695 StartZ=0 EndX=127.326 EndY=56.7187 EndZ=0
    g102: LineSegment StartX=125.607 StartY=54.1951 StartZ=0 EndX=61.5791 EndY=89.3511 EndZ=0
    g103: Circle CenterX=61.5791 CenterY=-56.9099 CenterZ=0 NormalX=0 NormalY=0 NormalZ=1 AngleXU=0 Radius=1
    g104: Circle CenterX=58.0728 CenterY=-58.8351 CenterZ=0 NormalX=0 NormalY=0 NormalZ=1 AngleXU=0 Radius=1
    g105: Circle CenterX=58.0728 CenterY=-62.8351 CenterZ=0 NormalX=0 NormalY=0 NormalZ=1 AngleXU=0 Radius=1
    g106: BSplineCurve PolesCount=3 KnotsCount=2 Degree=2 IsPeriodic=0
    g107: GeomPoint X=61.5791 Y=-56.9099 Z=0
    g108: GeomPoint X=58.0728 Y=-62.8351 Z=0
    g109: Circle CenterX=58.0728 CenterY=-77.8102 CenterZ=0 NormalX=0 NormalY=0 NormalZ=1 AngleXU=0 Radius=1
    g110: Circle CenterX=58.0728 CenterY=-81.8102 CenterZ=0 NormalX=0 NormalY=0 NormalZ=1 AngleXU=0 Radius=1
    g111: Circle CenterX=61.1496 CenterY=-79.2541 CenterZ=0 NormalX=0 NormalY=0 NormalZ=1 AngleXU=0 Radius=1
    g112: BSplineCurve PolesCount=3 KnotsCount=2 Degree=2 IsPeriodic=0
    g113: GeomPoint X=58.0728 Y=-77.8102 Z=0
    g114: GeomPoint X=61.1496 Y=-79.2541 Z=0
    g115: LineSegment StartX=58.0728 StartY=-62.8351 StartZ=0 EndX=58.0728 EndY=-77.8102 EndZ=0
    g116: LineSegment StartX=61.1496 StartY=-79.2541 StartZ=0 EndX=127.325 EndY=-24.2775 EndZ=0
    g117: LineSegment StartX=125.607 StartY=-21.7539 StartZ=0 EndX=61.5791 EndY=-56.9099 EndZ=0
    g118: Circle CenterX=302.567 CenterY=-56.9099 CenterZ=0 NormalX=0 NormalY=0 NormalZ=1 AngleXU=0 Radius=1
    g119: Circle CenterX=306.073 CenterY=-58.8351 CenterZ=0 NormalX=0 NormalY=0 NormalZ=1 AngleXU=0 Radius=1
    g120: Circle CenterX=306.073 CenterY=-62.8351 CenterZ=0 NormalX=0 NormalY=0 NormalZ=1 AngleXU=0 Radius=1
    g121: BSplineCurve PolesCount=3 KnotsCount=2 Degree=2 IsPeriodic=0
    g122: GeomPoint X=302.567 Y=-56.9099 Z=0
    g123: GeomPoint X=306.073 Y=-62.8351 Z=0
    g124: Circle CenterX=302.996 CenterY=-79.2541 CenterZ=0 NormalX=0 NormalY=0 NormalZ=1 AngleXU=0 Radius=1
    g125: Circle CenterX=306.073 CenterY=-81.8102 CenterZ=0 NormalX=0 NormalY=0 NormalZ=1 AngleXU=0 Radius=1
    g126: Circle CenterX=306.073 CenterY=-77.8102 CenterZ=0 NormalX=0 NormalY=0 NormalZ=1 AngleXU=0 Radius=1
    g127: BSplineCurve PolesCount=3 KnotsCount=2 Degree=2 IsPeriodic=0
    g128: GeomPoint X=302.996 Y=-79.2541 Z=0
    g129: GeomPoint X=306.073 Y=-77.8102 Z=0
    g130: LineSegment StartX=306.073 StartY=-62.8351 StartZ=0 EndX=306.073 EndY=-77.8102 EndZ=0
    g131: LineSegment StartX=302.996 StartY=-79.2541 StartZ=0 EndX=236.821 EndY=-24.2775 EndZ=0
    g132: LineSegment StartX=238.538 StartY=-21.7539 StartZ=0 EndX=302.567 EndY=-56.9099 EndZ=0
    g133: Circle CenterX=61.6457 CenterY=-88.8112 CenterZ=0 NormalX=0 NormalY=0 NormalZ=1 AngleXU=0 Radius=1
    g134: Circle CenterX=58.0728 CenterY=-91.7794 CenterZ=0 NormalX=0 NormalY=0 NormalZ=1 AngleXU=0 Radius=1
    g135: Circle CenterX=63.9135 CenterY=-91.7794 CenterZ=0 NormalX=0 NormalY=0 NormalZ=1 AngleXU=0 Radius=1
    g136: BSplineCurve PolesCount=3 KnotsCount=2 Degree=2 IsPeriodic=0
    g137: GeomPoint X=61.6457 Y=-88.8112 Z=0
    g138: GeomPoint X=63.9135 Y=-91.7794 Z=0
    g139: Circle CenterX=179.022 CenterY=-85.8163 CenterZ=0 NormalX=0 NormalY=0 NormalZ=1 AngleXU=0 Radius=1
    g140: Circle CenterX=179.022 CenterY=-91.7794 CenterZ=0 NormalX=0 NormalY=0 NormalZ=1 AngleXU=0 Radius=1
    g141: Circle CenterX=171.895 CenterY=-91.7794 CenterZ=0 NormalX=0 NormalY=0 NormalZ=1 AngleXU=0 Radius=1
    g142: BSplineCurve PolesCount=3 KnotsCount=2 Degree=2 IsPeriodic=0
    g143: GeomPoint X=179.022 Y=-85.8163 Z=0
    g144: GeomPoint X=171.895 Y=-91.7794 Z=0
    g145: Circle CenterX=185.124 CenterY=-86.2028 CenterZ=0 NormalX=0 NormalY=0 NormalZ=1 AngleXU=0 Radius=1
    g146: Circle CenterX=185.124 CenterY=-91.7794 CenterZ=0 NormalX=0 NormalY=0 NormalZ=1 AngleXU=0 Radius=1
    g147: Circle CenterX=191.747 CenterY=-91.7794 CenterZ=0 NormalX=0 NormalY=0 NormalZ=1 AngleXU=0 Radius=1
    g148: BSplineCurve PolesCount=3 KnotsCount=2 Degree=2 IsPeriodic=0
    g149: GeomPoint X=185.124 Y=-86.2028 Z=0
    g150: GeomPoint X=191.747 Y=-91.7794 Z=0
    g151: Circle CenterX=299.888 CenterY=-86.6413 CenterZ=0 NormalX=0 NormalY=0 NormalZ=1 AngleXU=0 Radius=1
    g152: Circle CenterX=306.073 CenterY=-91.7794 CenterZ=0 NormalX=0 NormalY=0 NormalZ=1 AngleXU=0 Radius=1
    g153: Circle CenterX=298.776 CenterY=-91.7794 CenterZ=0 NormalX=0 NormalY=0 NormalZ=1 AngleXU=0 Radius=1
    g154: BSplineCurve PolesCount=3 KnotsCount=2 Degree=2 IsPeriodic=0
    g155: GeomPoint X=299.888 Y=-86.6413 Z=0
    g156: GeomPoint X=298.776 Y=-91.7794 Z=0
    g157: LineSegment StartX=189.124 StartY=5.37834 StartZ=0 EndX=299.888 EndY=-86.6413 EndZ=0
    g158: LineSegment StartX=298.776 StartY=-91.7794 StartZ=0 EndX=191.747 EndY=-91.7794 EndZ=0
    g159: LineSegment StartX=185.124 StartY=-86.2028 StartZ=0 EndX=185.124 EndY=5.34704 EndZ=0
    g160: LineSegment StartX=179.022 StartY=5.34704 StartZ=0 EndX=179.022 EndY=-85.8163 EndZ=0
    g161: LineSegment StartX=171.895 StartY=-91.7794 StartZ=0 EndX=63.9135 EndY=-91.7794 EndZ=0
    g162: LineSegment StartX=61.6457 StartY=-88.8112 StartZ=0 EndX=175.022 EndY=5.37834 EndZ=0
    g163: Circle CenterX=302.073 CenterY=124.221 CenterZ=0 NormalX=0 NormalY=0 NormalZ=1 AngleXU=0 Radius=1
    g164: Circle CenterX=306.073 CenterY=124.221 CenterZ=0 NormalX=0 NormalY=0 NormalZ=1 AngleXU=0 Radius=1
    g165: Circle CenterX=302.996 CenterY=121.665 CenterZ=0 NormalX=0 NormalY=0 NormalZ=1 AngleXU=0 Radius=1
    g166: BSplineCurve PolesCount=3 KnotsCount=2 Degree=2 IsPeriodic=0
    g167: GeomPoint X=302.073 Y=124.221 Z=0
    g168: GeomPoint X=302.996 Y=121.665 Z=0
    g169: Circle CenterX=189.124 CenterY=124.221 CenterZ=0 NormalX=0 NormalY=0 NormalZ=1 AngleXU=0 Radius=1
    g170: Circle CenterX=185.124 CenterY=124.221 CenterZ=0 NormalX=0 NormalY=0 NormalZ=1 AngleXU=0 Radius=1
    g171: Circle CenterX=185.124 CenterY=120.221 CenterZ=0 NormalX=0 NormalY=0 NormalZ=1 AngleXU=0 Radius=1
    g172: BSplineCurve PolesCount=3 KnotsCount=2 Degree=2 IsPeriodic=0
    g173: GeomPoint X=189.124 Y=124.221 Z=0
    g174: GeomPoint X=185.124 Y=120.221 Z=0
    g175: Circle CenterX=175.022 CenterY=124.221 CenterZ=0 NormalX=0 NormalY=0 NormalZ=1 AngleXU=0 Radius=1
    g176: Circle CenterX=179.022 CenterY=124.221 CenterZ=0 NormalX=0 NormalY=0 NormalZ=1 AngleXU=0 Radius=1
    g177: Circle CenterX=179.022 CenterY=120.221 CenterZ=0 NormalX=0 NormalY=0 NormalZ=1 AngleXU=0 Radius=1
    g178: BSplineCurve PolesCount=3 KnotsCount=2 Degree=2 IsPeriodic=0
    g179: GeomPoint X=175.022 Y=124.221 Z=0
    g180: GeomPoint X=179.022 Y=120.221 Z=0
    g181: Circle CenterX=62.0728 CenterY=124.221 CenterZ=0 NormalX=0 NormalY=0 NormalZ=1 AngleXU=0 Radius=1
    g182: Circle CenterX=58.0728 CenterY=124.221 CenterZ=0 NormalX=0 NormalY=0 NormalZ=1 AngleXU=0 Radius=1
    g183: Circle CenterX=61.1496 CenterY=121.665 CenterZ=0 NormalX=0 NormalY=0 NormalZ=1 AngleXU=0 Radius=1
    g184: BSplineCurve PolesCount=3 KnotsCount=2 Degree=2 IsPeriodic=0
    g185: GeomPoint X=62.0728 Y=124.221 Z=0
    g186: GeomPoint X=61.1496 Y=121.665 Z=0
    g187: LineSegment StartX=62.0728 StartY=124.221 StartZ=0 EndX=175.022 EndY=124.221 EndZ=0
    g188: LineSegment StartX=179.022 StartY=120.221 StartZ=0 EndX=179.022 EndY=27.0628 EndZ=0
    g189: LineSegment StartX=185.124 StartY=27.0628 StartZ=0 EndX=185.124 EndY=120.221 EndZ=0
    g190: LineSegment StartX=189.124 StartY=124.221 StartZ=0 EndX=302.073 EndY=124.221 EndZ=0
    g191: LineSegment StartX=302.996 StartY=121.665 StartZ=0 EndX=189.124 EndY=27.0628 EndZ=0
    g192: LineSegment StartX=175.022 StartY=27.0628 StartZ=0 EndX=61.1496 EndY=121.665 EndZ=0
    g193: Circle CenterX=61.5791 CenterY=75.4095 CenterZ=0 NormalX=0 NormalY=0 NormalZ=1 AngleXU=0 Radius=1
    g194: Circle CenterX=58.0728 CenterY=77.3346 CenterZ=0 NormalX=0 NormalY=0 NormalZ=1 AngleXU=0 Radius=1
    g195: Circle CenterX=58.0728 CenterY=73.3346 CenterZ=0 NormalX=0 NormalY=0 NormalZ=1 AngleXU=0 Radius=1
    g196: BSplineCurve PolesCount=3 KnotsCount=2 Degree=2 IsPeriodic=0
    g197: GeomPoint X=61.5791 Y=75.4095 Z=0
    g198: GeomPoint X=58.0728 Y=73.3346 Z=0
    g199: Circle CenterX=58.0728 CenterY=-40.8935 CenterZ=0 NormalX=0 NormalY=0 NormalZ=1 AngleXU=0 Radius=1
    g200: Circle CenterX=58.0728 CenterY=-44.8935 CenterZ=0 NormalX=0 NormalY=0 NormalZ=1 AngleXU=0 Radius=1
    g201: Circle CenterX=61.5791 CenterY=-42.9683 CenterZ=0 NormalX=0 NormalY=0 NormalZ=1 AngleXU=0 Radius=1
    g202: BSplineCurve PolesCount=3 KnotsCount=2 Degree=2 IsPeriodic=0
    g203: GeomPoint X=58.0728 Y=-40.8935 Z=0
    g204: GeomPoint X=61.5791 Y=-42.9683 Z=0
    g205: LineSegment StartX=61.5791 StartY=-42.9683 StartZ=0 EndX=165.871 EndY=14.2954 EndZ=0
    g206: LineSegment StartX=165.871 StartY=18.1458 StartZ=0 EndX=61.5791 EndY=75.4095 EndZ=0
    g207: LineSegment StartX=58.0728 StartY=73.3346 StartZ=0 EndX=58.0728 EndY=-40.8935 EndZ=0
    g208: Circle CenterX=302.567 CenterY=-42.9683 CenterZ=0 NormalX=0 NormalY=0 NormalZ=1 AngleXU=0 Radius=1
    g209: Circle CenterX=306.073 CenterY=-44.8935 CenterZ=0 NormalX=0 NormalY=0 NormalZ=1 AngleXU=0 Radius=1
    g210: Circle CenterX=306.073 CenterY=-40.8935 CenterZ=0 NormalX=0 NormalY=0 NormalZ=1 AngleXU=0 Radius=1
    g211: BSplineCurve PolesCount=3 KnotsCount=2 Degree=2 IsPeriodic=0
    g212: GeomPoint X=302.567 Y=-42.9683 Z=0
    g213: GeomPoint X=306.073 Y=-40.8935 Z=0
    g214: Circle CenterX=306.073 CenterY=73.3346 CenterZ=0 NormalX=0 NormalY=0 NormalZ=1 AngleXU=0 Radius=1
    g215: Circle CenterX=306.073 CenterY=77.3346 CenterZ=0 NormalX=0 NormalY=0 NormalZ=1 AngleXU=0 Radius=1
    g216: Circle CenterX=302.567 CenterY=75.4095 CenterZ=0 NormalX=0 NormalY=0 NormalZ=1 AngleXU=0 Radius=1
    g217: BSplineCurve PolesCount=3 KnotsCount=2 Degree=2 IsPeriodic=0
    g218: GeomPoint X=306.073 Y=73.3346 Z=0
    g219: GeomPoint X=302.567 Y=75.4095 Z=0
    g220: LineSegment StartX=302.567 StartY=-42.9683 StartZ=0 EndX=198.275 EndY=14.2954 EndZ=0
    g221: LineSegment StartX=198.275 StartY=18.1458 StartZ=0 EndX=302.567 EndY=75.4095 EndZ=0
    g222: LineSegment StartX=306.073 StartY=73.3346 StartZ=0 EndX=306.073 EndY=-40.8935 EndZ=0
    g223: LineSegment StartX=322.073 StartY=105.865 StartZ=0 EndX=328.643 EndY=105.865 EndZ=0
    g224: LineSegment StartX=318.073 StartY=120.221 StartZ=0 EndX=318.073 EndY=109.865 EndZ=0
    g225: LineSegment StartX=336.157 StartY=107.779 StartZ=0 EndX=362.567 EndY=122.294 EndZ=0
    g226: Circle CenterX=362.073 CenterY=124.221 CenterZ=0 NormalX=0 NormalY=0 NormalZ=1 AngleXU=0 Radius=1
    g227: Circle CenterX=366.073 CenterY=124.221 CenterZ=0 NormalX=0 NormalY=0 NormalZ=1 AngleXU=0 Radius=1
    g228: Circle CenterX=362.567 CenterY=122.294 CenterZ=0 NormalX=0 NormalY=0 NormalZ=1 AngleXU=0 Radius=1
    g229: BSplineCurve PolesCount=3 KnotsCount=2 Degree=2 IsPeriodic=0
    g230: GeomPoint X=362.073 Y=124.221 Z=0
    g231: GeomPoint X=362.567 Y=122.294 Z=0
    g232: Circle CenterX=322.073 CenterY=124.221 CenterZ=0 NormalX=0 NormalY=0 NormalZ=1 AngleXU=0 Radius=1
    g233: Circle CenterX=318.073 CenterY=124.221 CenterZ=0 NormalX=0 NormalY=0 NormalZ=1 AngleXU=0 Radius=1
    g234: Circle CenterX=318.073 CenterY=120.221 CenterZ=0 NormalX=0 NormalY=0 NormalZ=1 AngleXU=0 Radius=1
    g235: BSplineCurve PolesCount=3 KnotsCount=2 Degree=2 IsPeriodic=0
    g236: GeomPoint X=322.073 Y=124.221 Z=0
    g237: GeomPoint X=318.073 Y=120.221 Z=0
    g238: Circle CenterX=322.073 CenterY=105.865 CenterZ=0 NormalX=0 NormalY=0 NormalZ=1 AngleXU=0 Radius=1
    g239: Circle CenterX=318.073 CenterY=105.865 CenterZ=0 NormalX=0 NormalY=0 NormalZ=1 AngleXU=0 Radius=1
    g240: Circle CenterX=318.073 CenterY=109.865 CenterZ=0 NormalX=0 NormalY=0 NormalZ=1 AngleXU=0 Radius=1
    g241: BSplineCurve PolesCount=3 KnotsCount=2 Degree=2 IsPeriodic=0
    g242: GeomPoint X=322.073 Y=105.865 Z=0
    g243: GeomPoint X=318.073 Y=109.865 Z=0
    g244: Circle CenterX=336.157 CenterY=107.779 CenterZ=0 NormalX=0 NormalY=0 NormalZ=1 AngleXU=0 Radius=1
    g245: Circle CenterX=332.651 CenterY=105.853 CenterZ=0 NormalX=0 NormalY=0 NormalZ=1 AngleXU=0 Radius=1
    g246: Circle CenterX=328.643 CenterY=105.865 CenterZ=0 NormalX=0 NormalY=0 NormalZ=1 AngleXU=0 Radius=1
    g247: BSplineCurve PolesCount=3 KnotsCount=2 Degree=2 IsPeriodic=0
    g248: GeomPoint X=336.157 Y=107.779 Z=0
    g249: GeomPoint X=328.643 Y=105.865 Z=0
    g250: LineSegment StartX=322.073 StartY=124.221 StartZ=0 EndX=362.073 EndY=124.221 EndZ=0
    g251: Circle CenterX=371.567 CenterY=-80.8644 CenterZ=0 NormalX=0 NormalY=0 NormalZ=1 AngleXU=0 Radius=1
    g252: Circle CenterX=375.073 CenterY=-82.7896 CenterZ=0 NormalX=0 NormalY=0 NormalZ=1 AngleXU=0 Radius=1
    g253: Circle CenterX=375.073 CenterY=-78.7896 CenterZ=0 NormalX=0 NormalY=0 NormalZ=1 AngleXU=0 Radius=1
    g254: BSplineCurve PolesCount=3 KnotsCount=2 Degree=2 IsPeriodic=0
    g255: GeomPoint X=371.567 Y=-80.8644 Z=0
    g256: GeomPoint X=375.073 Y=-78.7896 Z=0
    g257: Circle CenterX=321.579 CenterY=-53.4075 CenterZ=0 NormalX=0 NormalY=0 NormalZ=1 AngleXU=0 Radius=1
    g258: Circle CenterX=318.073 CenterY=-51.4823 CenterZ=0 NormalX=0 NormalY=0 NormalZ=1 AngleXU=0 Radius=1
    g259: Circle CenterX=318.073 CenterY=-47.4805 CenterZ=0 NormalX=0 NormalY=0 NormalZ=1 AngleXU=0 Radius=1
    g260: BSplineCurve PolesCount=3 KnotsCount=2 Degree=2 IsPeriodic=0
    g261: GeomPoint X=321.579 Y=-53.4075 Z=0
    g262: GeomPoint X=318.073 Y=-47.4805 Z=0
    g263: LineSegment StartX=371.567 StartY=-80.8644 StartZ=0 EndX=321.579 EndY=-53.4075 EndZ=0
    g264: Circle CenterX=321.579 CenterY=-67.3492 CenterZ=0 NormalX=0 NormalY=0 NormalZ=1 AngleXU=0 Radius=1
    g265: Circle CenterX=318.073 CenterY=-65.424 CenterZ=0 NormalX=0 NormalY=0 NormalZ=1 AngleXU=0 Radius=1
    g266: Circle CenterX=318.073 CenterY=-69.424 CenterZ=0 NormalX=0 NormalY=0 NormalZ=1 AngleXU=0 Radius=1
    g267: BSplineCurve PolesCount=3 KnotsCount=2 Degree=2 IsPeriodic=0
    g268: GeomPoint X=321.579 Y=-67.3492 Z=0
    g269: GeomPoint X=318.073 Y=-69.424 Z=0
    g270: Circle CenterX=362.567 CenterY=-89.8542 CenterZ=0 NormalX=0 NormalY=0 NormalZ=1 AngleXU=0 Radius=1
    g271: Circle CenterX=366.073 CenterY=-91.7794 CenterZ=0 NormalX=0 NormalY=0 NormalZ=1 AngleXU=0 Radius=1
    g272: Circle CenterX=362.073 CenterY=-91.7794 CenterZ=0 NormalX=0 NormalY=0 NormalZ=1 AngleXU=0 Radius=1
    g273: BSplineCurve PolesCount=3 KnotsCount=2 Degree=2 IsPeriodic=0
    g274: GeomPoint X=362.567 Y=-89.8542 Z=0
    g275: GeomPoint X=362.073 Y=-91.7794 Z=0
    g276: Circle CenterX=322.073 CenterY=-91.7794 CenterZ=0 NormalX=0 NormalY=0 NormalZ=1 AngleXU=0 Radius=1
    g277: Circle CenterX=318.073 CenterY=-91.7794 CenterZ=0 NormalX=0 NormalY=0 NormalZ=1 AngleXU=0 Radius=1
    g278: Circle CenterX=318.073 CenterY=-87.7794 CenterZ=0 NormalX=0 NormalY=0 NormalZ=1 AngleXU=0 Radius=1
    g279: BSplineCurve PolesCount=3 KnotsCount=2 Degree=2 IsPeriodic=0
    g280: GeomPoint X=322.073 Y=-91.7794 Z=0
    g281: GeomPoint X=318.073 Y=-87.7794 Z=0
    g282: LineSegment StartX=362.567 StartY=-89.8542 StartZ=0 EndX=321.579 EndY=-67.3492 EndZ=0
    g283: LineSegment StartX=318.073 StartY=-69.424 StartZ=0 EndX=318.073 EndY=-87.7794 EndZ=0
    g284: LineSegment StartX=322.073 StartY=-91.7794 StartZ=0 EndX=362.073 EndY=-91.7794 EndZ=0
    g285: Circle CenterX=2.07281 CenterY=124.221 CenterZ=0 NormalX=0 NormalY=0 NormalZ=1 AngleXU=0 Radius=1
    g286: Circle CenterX=1.57905 CenterY=122.295 CenterZ=0 NormalX=0 NormalY=0 NormalZ=1 AngleXU=0 Radius=1
    g287: BSplineCurve PolesCount=3 KnotsCount=2 Degree=2 IsPeriodic=0
    g288: GeomPoint X=2.07281 Y=124.221 Z=0
    g289: GeomPoint X=1.57905 Y=122.295 Z=0
    g290: Circle CenterX=42.0728 CenterY=124.221 CenterZ=0 NormalX=0 NormalY=0 NormalZ=1 AngleXU=0 Radius=1
    g291: Circle CenterX=46.0728 CenterY=124.221 CenterZ=0 NormalX=0 NormalY=0 NormalZ=1 AngleXU=0 Radius=1
    g292: Circle CenterX=46.0728 CenterY=120.221 CenterZ=0 NormalX=0 NormalY=0 NormalZ=1 AngleXU=0 Radius=1
    g293: BSplineCurve PolesCount=3 KnotsCount=2 Degree=2 IsPeriodic=0
    g294: GeomPoint X=42.0728 Y=124.221 Z=0
    g295: GeomPoint X=46.0728 Y=120.221 Z=0
    g296: Circle CenterX=46.0728 CenterY=109.865 CenterZ=0 NormalX=0 NormalY=0 NormalZ=1 AngleXU=0 Radius=1
    g297: Circle CenterX=46.0728 CenterY=105.865 CenterZ=0 NormalX=0 NormalY=0 NormalZ=1 AngleXU=0 Radius=1
    g298: Circle CenterX=42.0728 CenterY=105.865 CenterZ=0 NormalX=0 NormalY=0 NormalZ=1 AngleXU=0 Radius=1
    g299: BSplineCurve PolesCount=3 KnotsCount=2 Degree=2 IsPeriodic=0
    g300: GeomPoint X=46.0728 Y=109.865 Z=0
    g301: GeomPoint X=42.0728 Y=105.865 Z=0
    g302: Circle CenterX=35.5028 CenterY=105.865 CenterZ=0 NormalX=0 NormalY=0 NormalZ=1 AngleXU=0 Radius=1
    g303: Circle CenterX=31.5028 CenterY=105.865 CenterZ=0 NormalX=0 NormalY=0 NormalZ=1 AngleXU=0 Radius=1
    g304: Circle CenterX=27.9965 CenterY=107.79 CenterZ=0 NormalX=0 NormalY=0 NormalZ=1 AngleXU=0 Radius=1
    g305: BSplineCurve PolesCount=3 KnotsCount=2 Degree=2 IsPeriodic=0
    g306: GeomPoint X=35.5028 Y=105.865 Z=0
    g307: GeomPoint X=27.9965 Y=107.79 Z=0
    g308: LineSegment StartX=2.07281 StartY=124.221 StartZ=0 EndX=42.0728 EndY=124.221 EndZ=0
    g309: LineSegment StartX=46.0728 StartY=120.221 StartZ=0 EndX=46.0728 EndY=109.865 EndZ=0
    g310: LineSegment StartX=42.0728 StartY=105.865 StartZ=0 EndX=35.5028 EndY=105.865 EndZ=0
    g311: LineSegment StartX=27.9965 StartY=107.79 StartZ=0 EndX=1.57905 EndY=122.295 EndZ=0
    g312: Circle CenterX=42.5666 CenterY=-67.3492 CenterZ=0 NormalX=0 NormalY=0 NormalZ=1 AngleXU=0 Radius=1
    g313: Circle CenterX=46.0728 CenterY=-65.424 CenterZ=0 NormalX=0 NormalY=0 NormalZ=1 AngleXU=0 Radius=1
    g314: Circle CenterX=46.0728 CenterY=-69.424 CenterZ=0 NormalX=0 NormalY=0 NormalZ=1 AngleXU=0 Radius=1
    g315: BSplineCurve PolesCount=3 KnotsCount=2 Degree=2 IsPeriodic=0
    g316: GeomPoint X=42.5666 Y=-67.3492 Z=0
    g317: GeomPoint X=46.0728 Y=-69.424 Z=0
    g318: Circle CenterX=46.0728 CenterY=-87.7794 CenterZ=0 NormalX=0 NormalY=0 NormalZ=1 AngleXU=0 Radius=1
    g319: Circle CenterX=46.0728 CenterY=-91.7794 CenterZ=0 NormalX=0 NormalY=0 NormalZ=1 AngleXU=0 Radius=1
    g320: Circle CenterX=42.0728 CenterY=-91.7794 CenterZ=0 NormalX=0 NormalY=0 NormalZ=1 AngleXU=0 Radius=1
    g321: BSplineCurve PolesCount=3 KnotsCount=2 Degree=2 IsPeriodic=0
    g322: GeomPoint X=46.0728 Y=-87.7794 Z=0
    g323: GeomPoint X=42.0728 Y=-91.7794 Z=0
    g324: Circle CenterX=2.07281 CenterY=-91.7794 CenterZ=0 NormalX=0 NormalY=0 NormalZ=1 AngleXU=0 Radius=1
    g325: Circle CenterX=-1.92719 CenterY=-91.7794 CenterZ=0 NormalX=0 NormalY=0 NormalZ=1 AngleXU=0 Radius=1
    g326: Circle CenterX=1.57905 CenterY=-89.8542 CenterZ=0 NormalX=0 NormalY=0 NormalZ=1 AngleXU=0 Radius=1
    g327: BSplineCurve PolesCount=3 KnotsCount=2 Degree=2 IsPeriodic=0
    g328: GeomPoint X=2.07281 Y=-91.7794 Z=0
    g329: GeomPoint X=1.57905 Y=-89.8542 Z=0
    g330: LineSegment StartX=2.07281 StartY=-91.7794 StartZ=0 EndX=42.0728 EndY=-91.7794 EndZ=0
    g331: LineSegment StartX=46.0728 StartY=-87.7794 StartZ=0 EndX=46.0728 EndY=-69.424 EndZ=0
    g332: LineSegment StartX=42.5666 StartY=-67.3492 StartZ=0 EndX=1.57905 EndY=-89.8542 EndZ=0
    g333: Circle CenterX=322.073 CenterY=76.4095 CenterZ=0 NormalX=0 NormalY=0 NormalZ=1 AngleXU=0 Radius=4
    g334: BSplineCurve PolesCount=3 KnotsCount=2 Degree=2 IsPeriodic=0
    g335: GeomPoint X=318.073 Y=72.4095 Z=0
    g336: GeomPoint X=322.073 Y=76.4095 Z=0
    g337: Circle CenterX=375.073 CenterY=72.4095 CenterZ=0 NormalX=0 NormalY=0 NormalZ=1 AngleXU=0 Radius=1
    g338: Circle CenterX=375.073 CenterY=76.4095 CenterZ=0 NormalX=0 NormalY=0 NormalZ=1 AngleXU=0 Radius=1
    g339: Circle CenterX=371.073 CenterY=76.4095 CenterZ=0 NormalX=0 NormalY=0 NormalZ=1 AngleXU=0 Radius=1
    g340: BSplineCurve PolesCount=3 KnotsCount=2 Degree=2 IsPeriodic=0
    g341: GeomPoint X=375.073 Y=72.4095 Z=0
    g342: GeomPoint X=371.073 Y=76.4095 Z=0
    g343: LineSegment StartX=322.073 StartY=76.4095 StartZ=0 EndX=371.073 EndY=76.4095 EndZ=0
    g344: LineSegment StartX=318.073 StartY=72.4095 StartZ=0 EndX=318.073 EndY=-47.4805 EndZ=0
    g345: LineSegment StartX=375.073 StartY=72.4095 StartZ=0 EndX=375.073 EndY=-78.7896 EndZ=0
    g346: ArcOfCircle CenterX=-26.9272 CenterY=22.1087 CenterZ=0 NormalX=0 NormalY=0 NormalZ=1 AngleXU=0 Radius=4 StartAngle=5e-16 EndAngle=3.14159
    g347: LineSegment StartX=-22.9272 StartY=22.1087 StartZ=0 EndX=-18.9272 EndY=-83.7794 EndZ=0
    g348: LineSegment StartX=-34.9272 StartY=-83.7794 StartZ=0 EndX=-30.9272 EndY=22.1087 EndZ=0
  constraints (572):
    c: Coincident(g0,g2)
    c: Block(g0)
    c: Block(g1)
    c: Vertical(g3)
    c: Vertical(g4)
    c: Block(g4)
    c: Block(g3)
    c: Tangent(g6,g7) = 1.5708
    c: Tangent(g7,g9) = 1.5708
    c: Equal(g6,g9)
    c: Coincident(g8,g6)
    c: Coincident(g8,g9)
    c: Block(g7)
    c: Block(g8)
    c: Weight(g10) = 1
    c: Equal(g10,g11)
    c: Equal(g10,g12)
    c: InternalAlignment(g10,g13)
    c: InternalAlignment(g11,g13)
    c: InternalAlignment(g12,g13)
    c: InternalAlignment(g14,g13)
    c: InternalAlignment(g15,g13)
    c: Weight(g16) = 1
    c: Equal(g16,g17)
    c: Equal(g16,g18)
    c: InternalAlignment(g16,g19)
    c: InternalAlignment(g17,g19)
    c: InternalAlignment(g18,g19)
    c: InternalAlignment(g20,g19)
    c: InternalAlignment(g21,g19)
    c: Block(g19)
    c: Block(g13)
    c: Weight(g22) = 1
    c: Equal(g22,g23)
    c: Equal(g22,g24)
    c: InternalAlignment(g22,g25)
    c: InternalAlignment(g23,g25)
    c: InternalAlignment(g24,g25)
    c: InternalAlignment(g26,g25)
    c: InternalAlignment(g27,g25)
    c: Weight(g28) = 1
    c: Equal(g28,g29)
    c: Equal(g28,g30)
    c: InternalAlignment(g28,g31)
    c: InternalAlignment(g29,g31)
    c: InternalAlignment(g30,g31)
    c: InternalAlignment(g32,g31)
    c: InternalAlignment(g33,g31)
    c: Block(g31)
    c: Block(g25)
    c: Weight(g34) = 1
    c: Equal(g34,g35)
    c: Equal(g34,g36)
    c: InternalAlignment(g34,g37)
    c: InternalAlignment(g35,g37)
    c: InternalAlignment(g36,g37)
    c: InternalAlignment(g38,g37)
    c: InternalAlignment(g39,g37)
    c: Weight(g40) = 1
    c: Equal(g40,g41)
    c: Equal(g40,g42)
    c: InternalAlignment(g40,g43)
    c: InternalAlignment(g41,g43)
    c: InternalAlignment(g42,g43)
    c: InternalAlignment(g44,g43)
    c: InternalAlignment(g45,g43)
    c: Block(g37)
    c: Block(g43)
    c: Coincident(g46,g4)
    c: Coincident(g46,g3)
    c: Horizontal(g46)
    c: Distance(g46) = 450
    c: Coincident(g47,g4)
    c: Coincident(g47,g3)
    c: Horizontal(g47)
    c: Horizontal(g48)
    c: Coincident(g2,g48)
    c: Block(g48)
    c: Coincident(g1,g48)
    c: Weight(g49) = 1
    c: Equal(g49,g50)
    c: Equal(g49,g51)
    c: InternalAlignment(g49,g52)
    c: InternalAlignment(g50,g52)
    c: InternalAlignment(g51,g52)
    c: InternalAlignment(g53,g52)
    c: InternalAlignment(g54,g52)
    c: Block(g52)
    c: Weight(g55) = 1
    c: Equal(g55,g56)
    c: Equal(g55,g57)
    c: InternalAlignment(g55,g58)
    c: InternalAlignment(g56,g58)
    c: InternalAlignment(g57,g58)
    c: InternalAlignment(g59,g58)
    c: InternalAlignment(g60,g58)
    c: Block(g58)
    c: Weight(g61) = 1
    c: Equal(g61,g62)
    c: Equal(g61,g63)
    c: InternalAlignment(g61,g64)
    c: InternalAlignment(g62,g64)
    c: InternalAlignment(g63,g64)
    c: InternalAlignment(g65,g64)
    c: InternalAlignment(g66,g64)
    c: Block(g64)
    c: Weight(g67) = 1
    c: Equal(g67,g68)
    c: Equal(g67,g69)
    c: InternalAlignment(g67,g70)
    c: InternalAlignment(g68,g70)
    c: InternalAlignment(g69,g70)
    c: InternalAlignment(g71,g70)
    c: InternalAlignment(g72,g70)
    c: Block(g70)
    c: Weight(g73) = 1
    c: Equal(g73,g74)
    c: Equal(g73,g75)
    c: InternalAlignment(g73,g76)
    c: InternalAlignment(g74,g76)
    c: InternalAlignment(g75,g76)
    c: InternalAlignment(g77,g76)
    c: InternalAlignment(g78,g76)
    c: Weight(g79) = 1
    c: Equal(g79,g80)
    c: Equal(g79,g81)
    c: InternalAlignment(g79,g82)
    c: InternalAlignment(g80,g82)
    c: InternalAlignment(g81,g82)
    c: InternalAlignment(g83,g82)
    c: InternalAlignment(g84,g82)
    c: Block(g76)
    c: Block(g82)
    c: Coincident(g85,g76)
    c: Coincident(g85,g82)
    c: Vertical(g85)
    c: Coincident(g86,g76)
    c: Coincident(g86,g58)
    c: Coincident(g87,g58)
    c: Coincident(g87,g82)
    c: Weight(g88) = 1
    c: Equal(g88,g89)
    c: Equal(g88,g90)
    c: InternalAlignment(g88,g91)
    c: InternalAlignment(g89,g91)
    c: InternalAlignment(g90,g91)
    c: InternalAlignment(g92,g91)
    c: InternalAlignment(g93,g91)
    c: Weight(g94) = 1
    c: Equal(g94,g95)
    c: Equal(g94,g96)
    c: InternalAlignment(g94,g97)
    c: InternalAlignment(g95,g97)
    c: InternalAlignment(g96,g97)
    c: InternalAlignment(g98,g97)
    c: InternalAlignment(g99,g97)
    c: Block(g91)
    c: Block(g97)
    c: Coincident(g100,g91)
    c: Coincident(g100,g97)
    c: Vertical(g100)
    c: Coincident(g101,g91)
    c: Coincident(g101,g52)
    c: Coincident(g102,g52)
    c: Coincident(g102,g97)
    c: Weight(g103) = 1
    c: Equal(g103,g104)
    c: Equal(g103,g105)
    c: InternalAlignment(g103,g106)
    c: InternalAlignment(g104,g106)
    c: InternalAlignment(g105,g106)
    c: InternalAlignment(g107,g106)
    c: InternalAlignment(g108,g106)
    c: Weight(g109) = 1
    c: Equal(g109,g110)
    c: Equal(g109,g111)
    c: InternalAlignment(g109,g112)
    c: InternalAlignment(g110,g112)
    c: InternalAlignment(g111,g112)
    c: InternalAlignment(g113,g112)
    c: InternalAlignment(g114,g112)
    c: Block(g106)
    c: Block(g112)
    c: Coincident(g115,g106)
    c: Coincident(g115,g112)
    c: Vertical(g115)
    c: Coincident(g116,g112)
    c: Coincident(g116,g70)
    c: Coincident(g117,g70)
    c: Coincident(g117,g106)
    c: Weight(g118) = 1
    c: Equal(g118,g119)
    c: Equal(g118,g120)
    c: InternalAlignment(g118,g121)
    c: InternalAlignment(g119,g121)
    c: InternalAlignment(g120,g121)
    c: InternalAlignment(g122,g121)
    c: InternalAlignment(g123,g121)
    c: Weight(g124) = 1
    c: Equal(g124,g125)
    c: Equal(g124,g126)
    c: InternalAlignment(g124,g127)
    c: InternalAlignment(g125,g127)
    c: InternalAlignment(g126,g127)
    c: InternalAlignment(g128,g127)
    c: InternalAlignment(g129,g127)
    c: Block(g121)
    c: Block(g127)
    c: Coincident(g130,g121)
    c: Coincident(g130,g127)
    c: Vertical(g130)
    c: Coincident(g131,g127)
    c: Coincident(g131,g64)
    c: Coincident(g132,g64)
    c: Coincident(g132,g121)
    c: Weight(g133) = 1
    c: Equal(g133,g134)
    c: Equal(g133,g135)
    c: InternalAlignment(g133,g136)
    c: InternalAlignment(g134,g136)
    c: InternalAlignment(g135,g136)
    c: InternalAlignment(g137,g136)
    c: InternalAlignment(g138,g136)
    c: Weight(g139) = 1
    c: Equal(g139,g140)
    c: Equal(g139,g141)
    c: InternalAlignment(g139,g142)
    c: InternalAlignment(g140,g142)
    c: InternalAlignment(g141,g142)
    c: InternalAlignment(g143,g142)
    c: InternalAlignment(g144,g142)
    c: Weight(g145) = 1
    c: Equal(g145,g146)
    c: Equal(g145,g147)
    c: InternalAlignment(g145,g148)
    c: InternalAlignment(g146,g148)
    c: InternalAlignment(g147,g148)
    c: InternalAlignment(g149,g148)
    c: InternalAlignment(g150,g148)
    c: Weight(g151) = 1
    c: Equal(g151,g152)
    c: Equal(g151,g153)
    c: InternalAlignment(g151,g154)
    c: InternalAlignment(g152,g154)
    c: InternalAlignment(g153,g154)
    c: InternalAlignment(g155,g154)
    c: InternalAlignment(g156,g154)
    c: Block(g154)
    c: Block(g148)
    c: Block(g142)
    c: Block(g136)
    c: Coincident(g157,g31)
    c: Coincident(g157,g154)
    c: Coincident(g158,g154)
    c: Coincident(g158,g148)
    c: Horizontal(g158)
    c: Coincident(g159,g148)
    c: Coincident(g159,g31)
    c: Vertical(g159)
    c: Coincident(g160,g25)
    c: Coincident(g160,g142)
    c: Vertical(g160)
    c: Coincident(g161,g142)
    c: Coincident(g161,g136)
    c: Horizontal(g161)
    c: Coincident(g162,g136)
    c: Coincident(g162,g25)
    c: Weight(g163) = 1
    c: Equal(g163,g164)
    c: Equal(g163,g165)
    c: InternalAlignment(g163,g166)
    c: InternalAlignment(g164,g166)
    c: InternalAlignment(g165,g166)
    c: InternalAlignment(g167,g166)
    c: InternalAlignment(g168,g166)
    c: Weight(g169) = 1
    c: Equal(g169,g170)
    c: Equal(g169,g171)
    c: InternalAlignment(g169,g172)
    c: InternalAlignment(g170,g172)
    c: InternalAlignment(g171,g172)
    c: InternalAlignment(g173,g172)
    c: InternalAlignment(g174,g172)
    c: Weight(g175) = 1
    c: Equal(g175,g176)
    c: Equal(g175,g177)
    c: InternalAlignment(g175,g178)
    c: InternalAlignment(g176,g178)
    c: InternalAlignment(g177,g178)
    c: InternalAlignment(g179,g178)
    c: InternalAlignment(g180,g178)
    c: Weight(g181) = 1
    c: Equal(g181,g182)
    c: Equal(g181,g183)
    c: InternalAlignment(g181,g184)
    c: InternalAlignment(g182,g184)
    c: InternalAlignment(g183,g184)
    c: InternalAlignment(g185,g184)
    c: InternalAlignment(g186,g184)
    c: Block(g184)
    c: Block(g178)
    c: Block(g172)
    c: Block(g166)
    c: Coincident(g187,g184)
    c: Coincident(g187,g178)
    c: Horizontal(g187)
    c: Coincident(g188,g178)
    c: Coincident(g188,g13)
    c: Vertical(g188)
    c: Coincident(g189,g19)
    c: Coincident(g189,g172)
    c: Vertical(g189)
    c: Coincident(g190,g172)
    c: Coincident(g190,g166)
    c: Horizontal(g190)
    c: Coincident(g191,g166)
    c: Coincident(g191,g19)
    c: Coincident(g192,g13)
    c: Weight(g193) = 1
    c: Equal(g193,g194)
    c: Equal(g193,g195)
    c: InternalAlignment(g193,g196)
    c: InternalAlignment(g194,g196)
    c: InternalAlignment(g195,g196)
    c: InternalAlignment(g197,g196)
    c: InternalAlignment(g198,g196)
    c: Weight(g199) = 1
    c: Equal(g199,g200)
    c: Equal(g199,g201)
    c: InternalAlignment(g199,g202)
    c: InternalAlignment(g200,g202)
    c: InternalAlignment(g201,g202)
    c: InternalAlignment(g203,g202)
    c: InternalAlignment(g204,g202)
    c: Block(g202)
    c: Block(g196)
    c: Coincident(g205,g202)
    c: Coincident(g205,g37)
    c: Coincident(g206,g37)
    c: Coincident(g206,g196)
    c: Coincident(g207,g196)
    c: Coincident(g207,g202)
    c: Vertical(g207)
    c: Weight(g208) = 1
    c: Equal(g208,g209)
    c: Equal(g208,g210)
    c: InternalAlignment(g208,g211)
    c: InternalAlignment(g209,g211)
    c: InternalAlignment(g210,g211)
    c: InternalAlignment(g212,g211)
    c: InternalAlignment(g213,g211)
    c: Weight(g214) = 1
    c: Equal(g214,g215)
    c: Equal(g214,g216)
    c: InternalAlignment(g214,g217)
    c: InternalAlignment(g215,g217)
    c: InternalAlignment(g216,g217)
    c: InternalAlignment(g218,g217)
    c: InternalAlignment(g219,g217)
    c: Block(g217)
    c: Block(g211)
    c: Coincident(g220,g211)
    c: Coincident(g220,g43)
    c: Coincident(g221,g43)
    c: Coincident(g221,g217)
    c: Coincident(g222,g217)
    c: Coincident(g222,g211)
    c: Vertical(g222)
    c: Horizontal(g223)
    c: Block(g223)
    c: Vertical(g224)
    c: Block(g224)
    c: Block(g225)
    c: Weight(g226) = 1
    c: Equal(g226,g227)
    c: Equal(g226,g228)
    c: InternalAlignment(g226,g229)
    c: InternalAlignment(g227,g229)
    c: InternalAlignment(g228,g229)
    c: InternalAlignment(g230,g229)
    c: InternalAlignment(g231,g229)
    c: Weight(g232) = 1
    c: Equal(g232,g233)
    c: Equal(g232,g234)
    c: InternalAlignment(g232,g235)
    c: InternalAlignment(g233,g235)
    c: InternalAlignment(g234,g235)
    c: InternalAlignment(g236,g235)
    c: InternalAlignment(g237,g235)
    c: Weight(g238) = 1
    c: Equal(g238,g239)
    c: Equal(g238,g240)
    c: InternalAlignment(g238,g241)
    c: InternalAlignment(g239,g241)
    c: InternalAlignment(g240,g241)
    c: InternalAlignment(g242,g241)
    c: InternalAlignment(g243,g241)
    c: Weight(g244) = 1
    c: Equal(g244,g245)
    c: Equal(g244,g246)
    c: InternalAlignment(g244,g247)
    c: InternalAlignment(g245,g247)
    c: InternalAlignment(g246,g247)
    c: InternalAlignment(g248,g247)
    c: InternalAlignment(g249,g247)
    c: Block(g229)
    c: Block(g235)
    c: Block(g241)
    c: Block(g247)
    c: Coincident(g250,g235)
    c: Coincident(g250,g229)
    c: Horizontal(g250)
    c: Block(g192)
    c: Weight(g251) = 1
    c: Equal(g251,g252)
    c: Equal(g251,g253)
    c: InternalAlignment(g251,g254)
    c: InternalAlignment(g252,g254)
    c: InternalAlignment(g253,g254)
    c: InternalAlignment(g255,g254)
    c: InternalAlignment(g256,g254)
    c: Weight(g257) = 1
    c: Equal(g257,g258)
    c: Equal(g257,g259)
    c: InternalAlignment(g257,g260)
    c: InternalAlignment(g258,g260)
    c: InternalAlignment(g259,g260)
    c: InternalAlignment(g261,g260)
    c: InternalAlignment(g262,g260)
    c: Block(g254)
    c: Block(g260)
    c: Coincident(g263,g254)
    c: Coincident(g263,g260)
    c: Weight(g264) = 1
    c: Equal(g264,g265)
    c: Equal(g264,g266)
    c: InternalAlignment(g264,g267)
    c: InternalAlignment(g265,g267)
    c: InternalAlignment(g266,g267)
    c: InternalAlignment(g268,g267)
    c: InternalAlignment(g269,g267)
    c: Weight(g270) = 1
    c: Equal(g270,g271)
    c: Equal(g270,g272)
    c: InternalAlignment(g270,g273)
    c: InternalAlignment(g271,g273)
    c: InternalAlignment(g272,g273)
    c: InternalAlignment(g274,g273)
    c: InternalAlignment(g275,g273)
    c: Weight(g276) = 1
    c: Equal(g276,g277)
    c: Equal(g276,g278)
    c: InternalAlignment(g276,g279)
    c: InternalAlignment(g277,g279)
    c: InternalAlignment(g278,g279)
    c: InternalAlignment(g280,g279)
    c: InternalAlignment(g281,g279)
    c: Block(g279)
    c: Block(g273)
    c: Block(g267)
    c: Coincident(g282,g273)
    c: Coincident(g282,g267)
    c: Coincident(g283,g267)
    c: Coincident(g283,g279)
    c: Vertical(g283)
    c: Coincident(g284,g279)
    c: Coincident(g284,g273)
    c: Horizontal(g284)
    c: Weight(g285) = 1
    c: Equal(g285,g286)
    c: InternalAlignment(g285,g287)
    c: InternalAlignment(g286,g287)
    c: InternalAlignment(g288,g287)
    c: InternalAlignment(g289,g287)
    c: Weight(g290) = 1
    c: InternalAlignment(g291,g293)
    c: InternalAlignment(g292,g293)
    c: InternalAlignment(g294,g293)
    c: InternalAlignment(g295,g293)
    c: Weight(g296) = 1
    c: Equal(g296,g297)
    c: Equal(g296,g298)
    c: InternalAlignment(g296,g299)
    c: InternalAlignment(g297,g299)
    c: InternalAlignment(g298,g299)
    c: InternalAlignment(g300,g299)
    c: InternalAlignment(g301,g299)
    c: Equal(g302,g303)
    c: Equal(g302,g304)
    c: InternalAlignment(g302,g305)
    c: InternalAlignment(g303,g305)
    c: InternalAlignment(g304,g305)
    c: InternalAlignment(g306,g305)
    c: InternalAlignment(g307,g305)
    c: Block(g293)
    c: Block(g299)
    c: Block(g305)
    c: Block(g287)
    c: Coincident(g308,g287)
    c: Coincident(g308,g293)
    c: Horizontal(g308)
    c: Coincident(g309,g293)
    c: Coincident(g309,g299)
    c: Vertical(g309)
    c: Coincident(g310,g299)
    c: Coincident(g310,g305)
    c: Horizontal(g310)
    c: Coincident(g311,g305)
    c: Coincident(g311,g287)
    c: Weight(g312) = 1
    c: Equal(g312,g313)
    c: Equal(g312,g314)
    c: InternalAlignment(g312,g315)
    c: InternalAlignment(g313,g315)
    c: InternalAlignment(g314,g315)
    c: InternalAlignment(g316,g315)
    c: InternalAlignment(g317,g315)
    c: Weight(g318) = 1
    c: Equal(g318,g319)
    c: Equal(g318,g320)
    c: InternalAlignment(g318,g321)
    c: InternalAlignment(g319,g321)
    c: InternalAlignment(g320,g321)
    c: InternalAlignment(g322,g321)
    c: InternalAlignment(g323,g321)
    c: Weight(g324) = 1
    c: Equal(g324,g325)
    c: Equal(g324,g326)
    c: InternalAlignment(g324,g327)
    c: InternalAlignment(g325,g327)
    c: InternalAlignment(g326,g327)
    c: InternalAlignment(g328,g327)
    c: InternalAlignment(g329,g327)
    c: Block(g327)
    c: Block(g321)
    c: Block(g315)
    c: Coincident(g330,g327)
    c: Coincident(g330,g321)
    c: Horizontal(g330)
    c: Coincident(g331,g321)
    c: Coincident(g331,g315)
    c: Vertical(g331)
    c: Coincident(g332,g315)
    c: Coincident(g332,g327)
    c: InternalAlignment(g333,g334)
    c: InternalAlignment(g335,g334)
    c: InternalAlignment(g336,g334)
    c: Block(g334)
    c: Equal(g337,g338)
    c: Equal(g337,g339)
    c: InternalAlignment(g337,g340)
    c: InternalAlignment(g338,g340)
    c: InternalAlignment(g339,g340)
    c: InternalAlignment(g341,g340)
    c: InternalAlignment(g342,g340)
    c: Block(g340)
    c: Coincident(g343,g334)
    c: Horizontal(g343)
    c: Block(g343)
    c: Coincident(g344,g334)
    c: Coincident(g344,g260)
    c: Vertical(g344)
    c: Coincident(g345,g340)
    c: Coincident(g345,g254)
    c: Vertical(g345)
    c: Block(g346)
    c: Block(g5)
    c: Distance(g344) = 119.89
    c: Coincident(g347,g346)
    c: Coincident(g347,g5)
    c: Coincident(g348,g5)
    c: Coincident(g348,g346)
